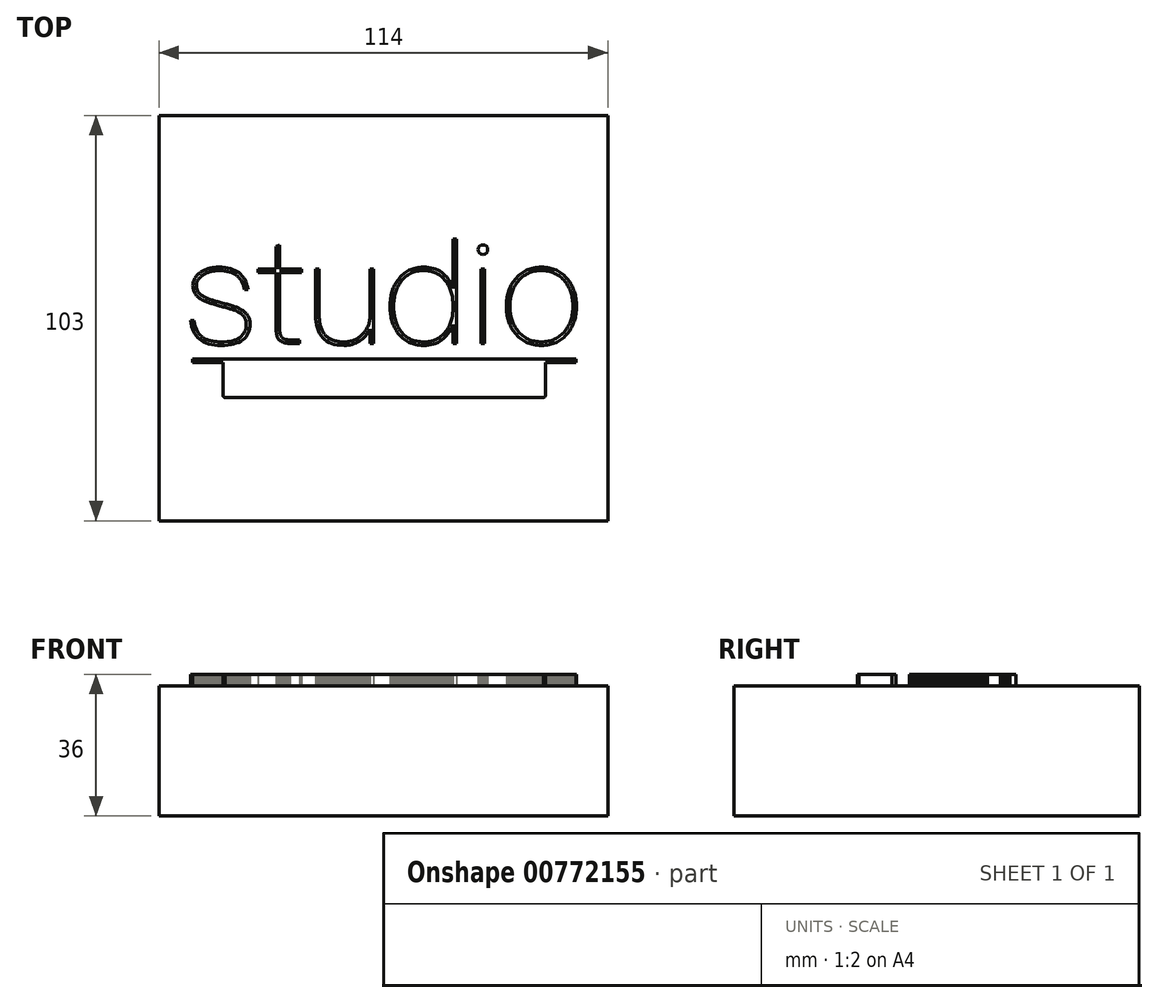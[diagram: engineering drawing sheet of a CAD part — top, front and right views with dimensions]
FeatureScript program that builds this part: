
annotation { "Feature Type Name" : "Feature", "Feature Type Description" : "" }
export const myFeature = defineFeature(function(context is Context, id is Id, definition is map)
    precondition{}
    {
        {
            var Q0;
            Q0=qCreatedBy(makeId("Top.planeOp"),FACE);
            var sketch = newSketch(context, id + "F0", { "sketchPlane" : qUnion([Q0])});
            skLineSegment(sketch, "E0", {"start": v(-48.1, -0.6) * mm, "end": v(-48.05, -0.96) * mm});
            skLineSegment(sketch, "E1", {"start": v(-48.05, -0.96) * mm, "end": v(-48, -1.3) * mm});
            skLineSegment(sketch, "E2", {"start": v(-48, -1.3) * mm, "end": v(-47.93, -1.64) * mm});
            skLineSegment(sketch, "E3", {"start": v(-47.93, -1.64) * mm, "end": v(-47.85, -1.96) * mm});
            skLineSegment(sketch, "E4", {"start": v(-47.85, -1.96) * mm, "end": v(-47.75, -2.27) * mm});
            skLineSegment(sketch, "E5", {"start": v(-47.75, -2.27) * mm, "end": v(-47.65, -2.56) * mm});
            skLineSegment(sketch, "E6", {"start": v(-47.65, -2.56) * mm, "end": v(-47.54, -2.85) * mm});
            skLineSegment(sketch, "E7", {"start": v(-47.54, -2.85) * mm, "end": v(-47.41, -3.12) * mm});
            skLineSegment(sketch, "E8", {"start": v(-47.41, -3.12) * mm, "end": v(-47.28, -3.38) * mm});
            skLineSegment(sketch, "E9", {"start": v(-47.28, -3.38) * mm, "end": v(-47.13, -3.62) * mm});
            skLineSegment(sketch, "E10", {"start": v(-47.13, -3.62) * mm, "end": v(-46.97, -3.86) * mm});
            skLineSegment(sketch, "E11", {"start": v(-46.97, -3.86) * mm, "end": v(-46.8, -4.08) * mm});
            skLineSegment(sketch, "E12", {"start": v(-46.8, -4.08) * mm, "end": v(-46.62, -4.29) * mm});
            skLineSegment(sketch, "E13", {"start": v(-46.62, -4.29) * mm, "end": v(-46.42, -4.48) * mm});
            skLineSegment(sketch, "E14", {"start": v(-46.42, -4.48) * mm, "end": v(-46.21, -4.67) * mm});
            skLineSegment(sketch, "E15", {"start": v(-46.21, -4.67) * mm, "end": v(-46, -4.84) * mm});
            skLineSegment(sketch, "E16", {"start": v(-46, -4.84) * mm, "end": v(-45.8, -4.98) * mm});
            skLineSegment(sketch, "E17", {"start": v(-45.8, -4.98) * mm, "end": v(-45.57, -5.12) * mm});
            skLineSegment(sketch, "E18", {"start": v(-45.57, -5.12) * mm, "end": v(-45.35, -5.25) * mm});
            skLineSegment(sketch, "E19", {"start": v(-45.35, -5.25) * mm, "end": v(-45.1, -5.36) * mm});
            skLineSegment(sketch, "E20", {"start": v(-45.1, -5.36) * mm, "end": v(-44.85, -5.47) * mm});
            skLineSegment(sketch, "E21", {"start": v(-44.85, -5.47) * mm, "end": v(-44.59, -5.57) * mm});
            skLineSegment(sketch, "E22", {"start": v(-44.59, -5.57) * mm, "end": v(-44.3, -5.66) * mm});
            skLineSegment(sketch, "E23", {"start": v(-44.3, -5.66) * mm, "end": v(-44.02, -5.74) * mm});
            skLineSegment(sketch, "E24", {"start": v(-44.02, -5.74) * mm, "end": v(-43.72, -5.81) * mm});
            skLineSegment(sketch, "E25", {"start": v(-43.72, -5.81) * mm, "end": v(-43.4, -5.87) * mm});
            skLineSegment(sketch, "E26", {"start": v(-43.4, -5.87) * mm, "end": v(-43.07, -5.92) * mm});
            skLineSegment(sketch, "E27", {"start": v(-43.07, -5.92) * mm, "end": v(-42.73, -5.97) * mm});
            skLineSegment(sketch, "E28", {"start": v(-42.73, -5.97) * mm, "end": v(-42.38, -6) * mm});
            skLineSegment(sketch, "E29", {"start": v(-42.38, -6) * mm, "end": v(-42.02, -6.02) * mm});
            skLineSegment(sketch, "E30", {"start": v(-42.02, -6.02) * mm, "end": v(-41.64, -6.04) * mm});
            skLineSegment(sketch, "E31", {"start": v(-41.64, -6.04) * mm, "end": v(-41.25, -6.04) * mm});
            skLineSegment(sketch, "E32", {"start": v(-41.25, -6.04) * mm, "end": v(-40.48, -6.02) * mm});
            skLineSegment(sketch, "E33", {"start": v(-40.48, -6.02) * mm, "end": v(-39.76, -5.97) * mm});
            skLineSegment(sketch, "E34", {"start": v(-39.76, -5.97) * mm, "end": v(-39.08, -5.88) * mm});
            skLineSegment(sketch, "E35", {"start": v(-39.08, -5.88) * mm, "end": v(-38.46, -5.75) * mm});
            skLineSegment(sketch, "E36", {"start": v(-38.46, -5.75) * mm, "end": v(-37.89, -5.58) * mm});
            skLineSegment(sketch, "E37", {"start": v(-37.89, -5.58) * mm, "end": v(-37.36, -5.38) * mm});
            skLineSegment(sketch, "E38", {"start": v(-37.36, -5.38) * mm, "end": v(-36.89, -5.14) * mm});
            skLineSegment(sketch, "E39", {"start": v(-36.89, -5.14) * mm, "end": v(-36.46, -4.87) * mm});
            skLineSegment(sketch, "E40", {"start": v(-36.46, -4.87) * mm, "end": v(-36.09, -4.56) * mm});
            skLineSegment(sketch, "E41", {"start": v(-36.09, -4.56) * mm, "end": v(-35.76, -4.21) * mm});
            skLineSegment(sketch, "E42", {"start": v(-35.76, -4.21) * mm, "end": v(-35.48, -3.83) * mm});
            skLineSegment(sketch, "E43", {"start": v(-35.48, -3.83) * mm, "end": v(-35.26, -3.41) * mm});
            skLineSegment(sketch, "E44", {"start": v(-35.26, -3.41) * mm, "end": v(-35.08, -2.95) * mm});
            skLineSegment(sketch, "E45", {"start": v(-35.08, -2.95) * mm, "end": v(-34.96, -2.46) * mm});
            skLineSegment(sketch, "E46", {"start": v(-34.96, -2.46) * mm, "end": v(-34.88, -1.94) * mm});
            skLineSegment(sketch, "E47", {"start": v(-34.88, -1.94) * mm, "end": v(-34.86, -1.37) * mm});
            skLineSegment(sketch, "E48", {"start": v(-34.86, -1.37) * mm, "end": v(-34.87, -1.13) * mm});
            skLineSegment(sketch, "E49", {"start": v(-34.87, -1.13) * mm, "end": v(-34.9, -0.9) * mm});
            skLineSegment(sketch, "E50", {"start": v(-34.9, -0.9) * mm, "end": v(-34.93, -0.67) * mm});
            skLineSegment(sketch, "E51", {"start": v(-34.93, -0.67) * mm, "end": v(-35, -0.45) * mm});
            skLineSegment(sketch, "E52", {"start": v(-35, -0.45) * mm, "end": v(-35.06, -0.24) * mm});
            skLineSegment(sketch, "E53", {"start": v(-35.06, -0.24) * mm, "end": v(-35.16, -0.03) * mm});
            skLineSegment(sketch, "E54", {"start": v(-35.16, -0.03) * mm, "end": v(-35.26, 0.17) * mm});
            skLineSegment(sketch, "E55", {"start": v(-35.26, 0.17) * mm, "end": v(-35.38, 0.36) * mm});
            skLineSegment(sketch, "E56", {"start": v(-35.38, 0.36) * mm, "end": v(-35.52, 0.54) * mm});
            skLineSegment(sketch, "E57", {"start": v(-35.52, 0.54) * mm, "end": v(-35.68, 0.71) * mm});
            skLineSegment(sketch, "E58", {"start": v(-35.68, 0.71) * mm, "end": v(-35.85, 0.88) * mm});
            skLineSegment(sketch, "E59", {"start": v(-35.85, 0.88) * mm, "end": v(-36.03, 1.04) * mm});
            skLineSegment(sketch, "E60", {"start": v(-36.03, 1.04) * mm, "end": v(-36.23, 1.2) * mm});
            skLineSegment(sketch, "E61", {"start": v(-36.23, 1.2) * mm, "end": v(-36.45, 1.34) * mm});
            skLineSegment(sketch, "E62", {"start": v(-36.45, 1.34) * mm, "end": v(-36.68, 1.48) * mm});
            skLineSegment(sketch, "E63", {"start": v(-36.68, 1.48) * mm, "end": v(-36.93, 1.62) * mm});
            skLineSegment(sketch, "E64", {"start": v(-36.93, 1.62) * mm, "end": v(-37.07, 1.69) * mm});
            skLineSegment(sketch, "E65", {"start": v(-37.07, 1.69) * mm, "end": v(-37.23, 1.76) * mm});
            skLineSegment(sketch, "E66", {"start": v(-37.23, 1.76) * mm, "end": v(-37.42, 1.84) * mm});
            skLineSegment(sketch, "E67", {"start": v(-37.42, 1.84) * mm, "end": v(-37.62, 1.92) * mm});
            skLineSegment(sketch, "E68", {"start": v(-37.62, 1.92) * mm, "end": v(-37.84, 2) * mm});
            skLineSegment(sketch, "E69", {"start": v(-37.84, 2) * mm, "end": v(-38.08, 2.09) * mm});
            skLineSegment(sketch, "E70", {"start": v(-38.08, 2.09) * mm, "end": v(-38.34, 2.18) * mm});
            skLineSegment(sketch, "E71", {"start": v(-38.34, 2.18) * mm, "end": v(-38.62, 2.27) * mm});
            skLineSegment(sketch, "E72", {"start": v(-38.62, 2.27) * mm, "end": v(-38.93, 2.37) * mm});
            skLineSegment(sketch, "E73", {"start": v(-38.93, 2.37) * mm, "end": v(-39.25, 2.46) * mm});
            skLineSegment(sketch, "E74", {"start": v(-39.25, 2.46) * mm, "end": v(-39.59, 2.57) * mm});
            skLineSegment(sketch, "E75", {"start": v(-39.59, 2.57) * mm, "end": v(-39.95, 2.67) * mm});
            skLineSegment(sketch, "E76", {"start": v(-39.95, 2.67) * mm, "end": v(-40.33, 2.78) * mm});
            skLineSegment(sketch, "E77", {"start": v(-40.33, 2.78) * mm, "end": v(-40.73, 2.89) * mm});
            skLineSegment(sketch, "E78", {"start": v(-40.73, 2.89) * mm, "end": v(-41.15, 3) * mm});
            skLineSegment(sketch, "E79", {"start": v(-41.15, 3) * mm, "end": v(-41.6, 3.11) * mm});
            skLineSegment(sketch, "E80", {"start": v(-41.6, 3.11) * mm, "end": v(-42, 3.22) * mm});
            skLineSegment(sketch, "E81", {"start": v(-42, 3.22) * mm, "end": v(-42.4, 3.33) * mm});
            skLineSegment(sketch, "E82", {"start": v(-42.4, 3.33) * mm, "end": v(-42.8, 3.44) * mm});
            skLineSegment(sketch, "E83", {"start": v(-42.8, 3.44) * mm, "end": v(-43.16, 3.55) * mm});
            skLineSegment(sketch, "E84", {"start": v(-43.16, 3.55) * mm, "end": v(-43.5, 3.66) * mm});
            skLineSegment(sketch, "E85", {"start": v(-43.5, 3.66) * mm, "end": v(-43.84, 3.77) * mm});
            skLineSegment(sketch, "E86", {"start": v(-43.84, 3.77) * mm, "end": v(-44.16, 3.87) * mm});
            skLineSegment(sketch, "E87", {"start": v(-44.16, 3.87) * mm, "end": v(-44.47, 3.98) * mm});
            skLineSegment(sketch, "E88", {"start": v(-44.47, 3.98) * mm, "end": v(-44.75, 4.09) * mm});
            skLineSegment(sketch, "E89", {"start": v(-44.75, 4.09) * mm, "end": v(-45.02, 4.2) * mm});
            skLineSegment(sketch, "E90", {"start": v(-45.02, 4.2) * mm, "end": v(-45.28, 4.3) * mm});
            skLineSegment(sketch, "E91", {"start": v(-45.28, 4.3) * mm, "end": v(-45.51, 4.4) * mm});
            skLineSegment(sketch, "E92", {"start": v(-45.51, 4.4) * mm, "end": v(-45.73, 4.5) * mm});
            skLineSegment(sketch, "E93", {"start": v(-45.73, 4.5) * mm, "end": v(-45.94, 4.6) * mm});
            skLineSegment(sketch, "E94", {"start": v(-45.94, 4.6) * mm, "end": v(-46.12, 4.7) * mm});
            skLineSegment(sketch, "E95", {"start": v(-46.12, 4.7) * mm, "end": v(-46.3, 4.8) * mm});
            skLineSegment(sketch, "E96", {"start": v(-46.3, 4.8) * mm, "end": v(-46.55, 4.95) * mm});
            skLineSegment(sketch, "E97", {"start": v(-46.55, 4.95) * mm, "end": v(-46.8, 5.12) * mm});
            skLineSegment(sketch, "E98", {"start": v(-46.8, 5.12) * mm, "end": v(-47.02, 5.3) * mm});
            skLineSegment(sketch, "E99", {"start": v(-47.02, 5.3) * mm, "end": v(-47.23, 5.48) * mm});
            skLineSegment(sketch, "E100", {"start": v(-47.23, 5.48) * mm, "end": v(-47.43, 5.67) * mm});
            skLineSegment(sketch, "E101", {"start": v(-47.43, 5.67) * mm, "end": v(-47.6, 5.87) * mm});
            skLineSegment(sketch, "E102", {"start": v(-47.6, 5.87) * mm, "end": v(-47.76, 6.08) * mm});
            skLineSegment(sketch, "E103", {"start": v(-47.76, 6.08) * mm, "end": v(-47.9, 6.3) * mm});
            skLineSegment(sketch, "E104", {"start": v(-47.9, 6.3) * mm, "end": v(-48.03, 6.51) * mm});
            skLineSegment(sketch, "E105", {"start": v(-48.03, 6.51) * mm, "end": v(-48.14, 6.74) * mm});
            skLineSegment(sketch, "E106", {"start": v(-48.14, 6.74) * mm, "end": v(-48.23, 6.98) * mm});
            skLineSegment(sketch, "E107", {"start": v(-48.23, 6.98) * mm, "end": v(-48.3, 7.22) * mm});
            skLineSegment(sketch, "E108", {"start": v(-48.3, 7.22) * mm, "end": v(-48.36, 7.47) * mm});
            skLineSegment(sketch, "E109", {"start": v(-48.36, 7.47) * mm, "end": v(-48.4, 7.72) * mm});
            skLineSegment(sketch, "E110", {"start": v(-48.4, 7.72) * mm, "end": v(-48.43, 7.99) * mm});
            skLineSegment(sketch, "E111", {"start": v(-48.43, 7.99) * mm, "end": v(-48.44, 8.26) * mm});
            skLineSegment(sketch, "E112", {"start": v(-48.44, 8.26) * mm, "end": v(-48.43, 8.51) * mm});
            skLineSegment(sketch, "E113", {"start": v(-48.43, 8.51) * mm, "end": v(-48.4, 8.77) * mm});
            skLineSegment(sketch, "E114", {"start": v(-48.4, 8.77) * mm, "end": v(-48.37, 9.01) * mm});
            skLineSegment(sketch, "E115", {"start": v(-48.37, 9.01) * mm, "end": v(-48.31, 9.25) * mm});
            skLineSegment(sketch, "E116", {"start": v(-48.31, 9.25) * mm, "end": v(-48.24, 9.49) * mm});
            skLineSegment(sketch, "E117", {"start": v(-48.24, 9.49) * mm, "end": v(-48.15, 9.72) * mm});
            skLineSegment(sketch, "E118", {"start": v(-48.15, 9.72) * mm, "end": v(-48.05, 9.94) * mm});
            skLineSegment(sketch, "E119", {"start": v(-48.05, 9.94) * mm, "end": v(-47.93, 10.16) * mm});
            skLineSegment(sketch, "E120", {"start": v(-47.93, 10.16) * mm, "end": v(-47.8, 10.37) * mm});
            skLineSegment(sketch, "E121", {"start": v(-47.8, 10.37) * mm, "end": v(-47.65, 10.58) * mm});
            skLineSegment(sketch, "E122", {"start": v(-47.65, 10.58) * mm, "end": v(-47.48, 10.78) * mm});
            skLineSegment(sketch, "E123", {"start": v(-47.48, 10.78) * mm, "end": v(-47.3, 10.97) * mm});
            skLineSegment(sketch, "E124", {"start": v(-47.3, 10.97) * mm, "end": v(-47.1, 11.16) * mm});
            skLineSegment(sketch, "E125", {"start": v(-47.1, 11.16) * mm, "end": v(-46.88, 11.34) * mm});
            skLineSegment(sketch, "E126", {"start": v(-46.88, 11.34) * mm, "end": v(-46.65, 11.52) * mm});
            skLineSegment(sketch, "E127", {"start": v(-46.65, 11.52) * mm, "end": v(-46.4, 11.68) * mm});
            skLineSegment(sketch, "E128", {"start": v(-46.4, 11.68) * mm, "end": v(-46.16, 11.84) * mm});
            skLineSegment(sketch, "E129", {"start": v(-46.16, 11.84) * mm, "end": v(-45.92, 12) * mm});
            skLineSegment(sketch, "E130", {"start": v(-45.92, 12) * mm, "end": v(-45.66, 12.13) * mm});
            skLineSegment(sketch, "E131", {"start": v(-45.66, 12.13) * mm, "end": v(-45.4, 12.25) * mm});
            skLineSegment(sketch, "E132", {"start": v(-45.4, 12.25) * mm, "end": v(-45.13, 12.37) * mm});
            skLineSegment(sketch, "E133", {"start": v(-45.13, 12.37) * mm, "end": v(-44.86, 12.47) * mm});
            skLineSegment(sketch, "E134", {"start": v(-44.86, 12.47) * mm, "end": v(-44.58, 12.57) * mm});
            skLineSegment(sketch, "E135", {"start": v(-44.58, 12.57) * mm, "end": v(-44.3, 12.65) * mm});
            skLineSegment(sketch, "E136", {"start": v(-44.3, 12.65) * mm, "end": v(-44, 12.72) * mm});
            skLineSegment(sketch, "E137", {"start": v(-44, 12.72) * mm, "end": v(-43.7, 12.79) * mm});
            skLineSegment(sketch, "E138", {"start": v(-43.7, 12.79) * mm, "end": v(-43.4, 12.84) * mm});
            skLineSegment(sketch, "E139", {"start": v(-43.4, 12.84) * mm, "end": v(-43.09, 12.89) * mm});
            skLineSegment(sketch, "E140", {"start": v(-43.09, 12.89) * mm, "end": v(-42.77, 12.92) * mm});
            skLineSegment(sketch, "E141", {"start": v(-42.77, 12.92) * mm, "end": v(-42.45, 12.94) * mm});
            skLineSegment(sketch, "E142", {"start": v(-42.45, 12.94) * mm, "end": v(-42.12, 12.96) * mm});
            skLineSegment(sketch, "E143", {"start": v(-42.12, 12.96) * mm, "end": v(-41.78, 12.96) * mm});
            skLineSegment(sketch, "E144", {"start": v(-41.78, 12.96) * mm, "end": v(-41, 12.94) * mm});
            skLineSegment(sketch, "E145", {"start": v(-41, 12.94) * mm, "end": v(-40.26, 12.87) * mm});
            skLineSegment(sketch, "E146", {"start": v(-40.26, 12.87) * mm, "end": v(-39.56, 12.76) * mm});
            skLineSegment(sketch, "E147", {"start": v(-39.56, 12.76) * mm, "end": v(-38.9, 12.6) * mm});
            skLineSegment(sketch, "E148", {"start": v(-38.9, 12.6) * mm, "end": v(-38.3, 12.4) * mm});
            skLineSegment(sketch, "E149", {"start": v(-38.3, 12.4) * mm, "end": v(-37.73, 12.16) * mm});
            skLineSegment(sketch, "E150", {"start": v(-37.73, 12.16) * mm, "end": v(-37.2, 11.87) * mm});
            skLineSegment(sketch, "E151", {"start": v(-37.2, 11.87) * mm, "end": v(-36.73, 11.54) * mm});
            skLineSegment(sketch, "E152", {"start": v(-36.73, 11.54) * mm, "end": v(-36.3, 11.16) * mm});
            skLineSegment(sketch, "E153", {"start": v(-36.3, 11.16) * mm, "end": v(-35.9, 10.74) * mm});
            skLineSegment(sketch, "E154", {"start": v(-35.9, 10.74) * mm, "end": v(-35.55, 10.27) * mm});
            skLineSegment(sketch, "E155", {"start": v(-35.55, 10.27) * mm, "end": v(-35.24, 9.76) * mm});
            skLineSegment(sketch, "E156", {"start": v(-35.24, 9.76) * mm, "end": v(-34.98, 9.2) * mm});
            skLineSegment(sketch, "E157", {"start": v(-34.98, 9.2) * mm, "end": v(-34.76, 8.6) * mm});
            skLineSegment(sketch, "E158", {"start": v(-34.76, 8.6) * mm, "end": v(-34.58, 7.96) * mm});
            skLineSegment(sketch, "E159", {"start": v(-34.58, 7.96) * mm, "end": v(-34.44, 7.27) * mm});
            skLineSegment(sketch, "E160", {"start": v(-34.44, 7.27) * mm, "end": v(-35.35, 7.27) * mm});
            skLineSegment(sketch, "E161", {"start": v(-35.35, 7.27) * mm, "end": v(-35.4, 7.55) * mm});
            skLineSegment(sketch, "E162", {"start": v(-35.4, 7.55) * mm, "end": v(-35.46, 7.83) * mm});
            skLineSegment(sketch, "E163", {"start": v(-35.46, 7.83) * mm, "end": v(-35.53, 8.1) * mm});
            skLineSegment(sketch, "E164", {"start": v(-35.53, 8.1) * mm, "end": v(-35.6, 8.35) * mm});
            skLineSegment(sketch, "E165", {"start": v(-35.6, 8.35) * mm, "end": v(-35.7, 8.6) * mm});
            skLineSegment(sketch, "E166", {"start": v(-35.7, 8.6) * mm, "end": v(-35.79, 8.83) * mm});
            skLineSegment(sketch, "E167", {"start": v(-35.79, 8.83) * mm, "end": v(-35.89, 9.06) * mm});
            skLineSegment(sketch, "E168", {"start": v(-35.89, 9.06) * mm, "end": v(-36, 9.28) * mm});
            skLineSegment(sketch, "E169", {"start": v(-36, 9.28) * mm, "end": v(-36.11, 9.49) * mm});
            skLineSegment(sketch, "E170", {"start": v(-36.11, 9.49) * mm, "end": v(-36.24, 9.7) * mm});
            skLineSegment(sketch, "E171", {"start": v(-36.24, 9.7) * mm, "end": v(-36.37, 9.89) * mm});
            skLineSegment(sketch, "E172", {"start": v(-36.37, 9.89) * mm, "end": v(-36.51, 10.07) * mm});
            skLineSegment(sketch, "E173", {"start": v(-36.51, 10.07) * mm, "end": v(-36.66, 10.25) * mm});
            skLineSegment(sketch, "E174", {"start": v(-36.66, 10.25) * mm, "end": v(-36.82, 10.42) * mm});
            skLineSegment(sketch, "E175", {"start": v(-36.82, 10.42) * mm, "end": v(-36.98, 10.58) * mm});
            skLineSegment(sketch, "E176", {"start": v(-36.98, 10.58) * mm, "end": v(-37.15, 10.74) * mm});
            skLineSegment(sketch, "E177", {"start": v(-37.15, 10.74) * mm, "end": v(-37.37, 10.9) * mm});
            skLineSegment(sketch, "E178", {"start": v(-37.37, 10.9) * mm, "end": v(-37.6, 11.06) * mm});
            skLineSegment(sketch, "E179", {"start": v(-37.6, 11.06) * mm, "end": v(-37.83, 11.2) * mm});
            skLineSegment(sketch, "E180", {"start": v(-37.83, 11.2) * mm, "end": v(-38.08, 11.33) * mm});
            skLineSegment(sketch, "E181", {"start": v(-38.08, 11.33) * mm, "end": v(-38.33, 11.45) * mm});
            skLineSegment(sketch, "E182", {"start": v(-38.33, 11.45) * mm, "end": v(-38.6, 11.56) * mm});
            skLineSegment(sketch, "E183", {"start": v(-38.6, 11.56) * mm, "end": v(-38.87, 11.66) * mm});
            skLineSegment(sketch, "E184", {"start": v(-38.87, 11.66) * mm, "end": v(-39.16, 11.75) * mm});
            skLineSegment(sketch, "E185", {"start": v(-39.16, 11.75) * mm, "end": v(-39.45, 11.83) * mm});
            skLineSegment(sketch, "E186", {"start": v(-39.45, 11.83) * mm, "end": v(-39.75, 11.9) * mm});
            skLineSegment(sketch, "E187", {"start": v(-39.75, 11.9) * mm, "end": v(-40.07, 11.96) * mm});
            skLineSegment(sketch, "E188", {"start": v(-40.07, 11.96) * mm, "end": v(-40.4, 12) * mm});
            skLineSegment(sketch, "E189", {"start": v(-40.4, 12) * mm, "end": v(-40.72, 12.04) * mm});
            skLineSegment(sketch, "E190", {"start": v(-40.72, 12.04) * mm, "end": v(-41.07, 12.07) * mm});
            skLineSegment(sketch, "E191", {"start": v(-41.07, 12.07) * mm, "end": v(-41.42, 12.08) * mm});
            skLineSegment(sketch, "E192", {"start": v(-41.42, 12.08) * mm, "end": v(-41.78, 12.09) * mm});
            skLineSegment(sketch, "E193", {"start": v(-41.78, 12.09) * mm, "end": v(-42.09, 12.08) * mm});
            skLineSegment(sketch, "E194", {"start": v(-42.09, 12.08) * mm, "end": v(-42.39, 12.07) * mm});
            skLineSegment(sketch, "E195", {"start": v(-42.39, 12.07) * mm, "end": v(-42.68, 12.05) * mm});
            skLineSegment(sketch, "E196", {"start": v(-42.68, 12.05) * mm, "end": v(-42.97, 12.02) * mm});
            skLineSegment(sketch, "E197", {"start": v(-42.97, 12.02) * mm, "end": v(-43.25, 11.98) * mm});
            skLineSegment(sketch, "E198", {"start": v(-43.25, 11.98) * mm, "end": v(-43.52, 11.93) * mm});
            skLineSegment(sketch, "E199", {"start": v(-43.52, 11.93) * mm, "end": v(-43.78, 11.87) * mm});
            skLineSegment(sketch, "E200", {"start": v(-43.78, 11.87) * mm, "end": v(-44.04, 11.8) * mm});
            skLineSegment(sketch, "E201", {"start": v(-44.04, 11.8) * mm, "end": v(-44.3, 11.73) * mm});
            skLineSegment(sketch, "E202", {"start": v(-44.3, 11.73) * mm, "end": v(-44.54, 11.65) * mm});
            skLineSegment(sketch, "E203", {"start": v(-44.54, 11.65) * mm, "end": v(-44.78, 11.56) * mm});
            skLineSegment(sketch, "E204", {"start": v(-44.78, 11.56) * mm, "end": v(-45.01, 11.46) * mm});
            skLineSegment(sketch, "E205", {"start": v(-45.01, 11.46) * mm, "end": v(-45.24, 11.34) * mm});
            skLineSegment(sketch, "E206", {"start": v(-45.24, 11.34) * mm, "end": v(-45.46, 11.22) * mm});
            skLineSegment(sketch, "E207", {"start": v(-45.46, 11.22) * mm, "end": v(-45.67, 11.1) * mm});
            skLineSegment(sketch, "E208", {"start": v(-45.67, 11.1) * mm, "end": v(-45.88, 10.96) * mm});
            skLineSegment(sketch, "E209", {"start": v(-45.88, 10.96) * mm, "end": v(-46.09, 10.82) * mm});
            skLineSegment(sketch, "E210", {"start": v(-46.09, 10.82) * mm, "end": v(-46.28, 10.67) * mm});
            skLineSegment(sketch, "E211", {"start": v(-46.28, 10.67) * mm, "end": v(-46.45, 10.53) * mm});
            skLineSegment(sketch, "E212", {"start": v(-46.45, 10.53) * mm, "end": v(-46.62, 10.38) * mm});
            skLineSegment(sketch, "E213", {"start": v(-46.62, 10.38) * mm, "end": v(-46.77, 10.23) * mm});
            skLineSegment(sketch, "E214", {"start": v(-46.77, 10.23) * mm, "end": v(-46.9, 10.07) * mm});
            skLineSegment(sketch, "E215", {"start": v(-46.9, 10.07) * mm, "end": v(-47.02, 9.9) * mm});
            skLineSegment(sketch, "E216", {"start": v(-47.02, 9.9) * mm, "end": v(-47.13, 9.74) * mm});
            skLineSegment(sketch, "E217", {"start": v(-47.13, 9.74) * mm, "end": v(-47.23, 9.57) * mm});
            skLineSegment(sketch, "E218", {"start": v(-47.23, 9.57) * mm, "end": v(-47.31, 9.4) * mm});
            skLineSegment(sketch, "E219", {"start": v(-47.31, 9.4) * mm, "end": v(-47.38, 9.22) * mm});
            skLineSegment(sketch, "E220", {"start": v(-47.38, 9.22) * mm, "end": v(-47.44, 9.04) * mm});
            skLineSegment(sketch, "E221", {"start": v(-47.44, 9.04) * mm, "end": v(-47.48, 8.85) * mm});
            skLineSegment(sketch, "E222", {"start": v(-47.48, 8.85) * mm, "end": v(-47.51, 8.66) * mm});
            skLineSegment(sketch, "E223", {"start": v(-47.51, 8.66) * mm, "end": v(-47.53, 8.46) * mm});
            skLineSegment(sketch, "E224", {"start": v(-47.53, 8.46) * mm, "end": v(-47.54, 8.26) * mm});
            skLineSegment(sketch, "E225", {"start": v(-47.54, 8.26) * mm, "end": v(-47.53, 8.04) * mm});
            skLineSegment(sketch, "E226", {"start": v(-47.53, 8.04) * mm, "end": v(-47.5, 7.83) * mm});
            skLineSegment(sketch, "E227", {"start": v(-47.5, 7.83) * mm, "end": v(-47.47, 7.63) * mm});
            skLineSegment(sketch, "E228", {"start": v(-47.47, 7.63) * mm, "end": v(-47.42, 7.43) * mm});
            skLineSegment(sketch, "E229", {"start": v(-47.42, 7.43) * mm, "end": v(-47.36, 7.23) * mm});
            skLineSegment(sketch, "E230", {"start": v(-47.36, 7.23) * mm, "end": v(-47.28, 7.05) * mm});
            skLineSegment(sketch, "E231", {"start": v(-47.28, 7.05) * mm, "end": v(-47.18, 6.87) * mm});
            skLineSegment(sketch, "E232", {"start": v(-47.18, 6.87) * mm, "end": v(-47.08, 6.69) * mm});
            skLineSegment(sketch, "E233", {"start": v(-47.08, 6.69) * mm, "end": v(-46.95, 6.52) * mm});
            skLineSegment(sketch, "E234", {"start": v(-46.95, 6.52) * mm, "end": v(-46.81, 6.35) * mm});
            skLineSegment(sketch, "E235", {"start": v(-46.81, 6.35) * mm, "end": v(-46.66, 6.19) * mm});
            skLineSegment(sketch, "E236", {"start": v(-46.66, 6.19) * mm, "end": v(-46.49, 6.03) * mm});
            skLineSegment(sketch, "E237", {"start": v(-46.49, 6.03) * mm, "end": v(-46.3, 5.88) * mm});
            skLineSegment(sketch, "E238", {"start": v(-46.3, 5.88) * mm, "end": v(-46.1, 5.73) * mm});
            skLineSegment(sketch, "E239", {"start": v(-46.1, 5.73) * mm, "end": v(-45.89, 5.59) * mm});
            skLineSegment(sketch, "E240", {"start": v(-45.89, 5.59) * mm, "end": v(-45.66, 5.45) * mm});
            skLineSegment(sketch, "E241", {"start": v(-45.66, 5.45) * mm, "end": v(-45.5, 5.37) * mm});
            skLineSegment(sketch, "E242", {"start": v(-45.5, 5.37) * mm, "end": v(-45.33, 5.28) * mm});
            skLineSegment(sketch, "E243", {"start": v(-45.33, 5.28) * mm, "end": v(-45.14, 5.2) * mm});
            skLineSegment(sketch, "E244", {"start": v(-45.14, 5.2) * mm, "end": v(-44.94, 5.1) * mm});
            skLineSegment(sketch, "E245", {"start": v(-44.94, 5.1) * mm, "end": v(-44.73, 5.02) * mm});
            skLineSegment(sketch, "E246", {"start": v(-44.73, 5.02) * mm, "end": v(-44.5, 4.93) * mm});
            skLineSegment(sketch, "E247", {"start": v(-44.5, 4.93) * mm, "end": v(-44.25, 4.84) * mm});
            skLineSegment(sketch, "E248", {"start": v(-44.25, 4.84) * mm, "end": v(-44, 4.75) * mm});
            skLineSegment(sketch, "E249", {"start": v(-44, 4.75) * mm, "end": v(-43.72, 4.65) * mm});
            skLineSegment(sketch, "E250", {"start": v(-43.72, 4.65) * mm, "end": v(-43.43, 4.56) * mm});
            skLineSegment(sketch, "E251", {"start": v(-43.43, 4.56) * mm, "end": v(-43.13, 4.47) * mm});
            skLineSegment(sketch, "E252", {"start": v(-43.13, 4.47) * mm, "end": v(-42.81, 4.37) * mm});
            skLineSegment(sketch, "E253", {"start": v(-42.81, 4.37) * mm, "end": v(-42.48, 4.28) * mm});
            skLineSegment(sketch, "E254", {"start": v(-42.48, 4.28) * mm, "end": v(-42.14, 4.18) * mm});
            skLineSegment(sketch, "E255", {"start": v(-42.14, 4.18) * mm, "end": v(-41.78, 4.08) * mm});
            skLineSegment(sketch, "E256", {"start": v(-41.78, 4.08) * mm, "end": v(-41.4, 3.99) * mm});
            skLineSegment(sketch, "E257", {"start": v(-41.4, 3.99) * mm, "end": v(-40.95, 3.87) * mm});
            skLineSegment(sketch, "E258", {"start": v(-40.95, 3.87) * mm, "end": v(-40.5, 3.76) * mm});
            skLineSegment(sketch, "E259", {"start": v(-40.5, 3.76) * mm, "end": v(-40.09, 3.64) * mm});
            skLineSegment(sketch, "E260", {"start": v(-40.09, 3.64) * mm, "end": v(-39.68, 3.53) * mm});
            skLineSegment(sketch, "E261", {"start": v(-39.68, 3.53) * mm, "end": v(-39.3, 3.42) * mm});
            skLineSegment(sketch, "E262", {"start": v(-39.3, 3.42) * mm, "end": v(-38.93, 3.3) * mm});
            skLineSegment(sketch, "E263", {"start": v(-38.93, 3.3) * mm, "end": v(-38.58, 3.2) * mm});
            skLineSegment(sketch, "E264", {"start": v(-38.58, 3.2) * mm, "end": v(-38.25, 3.1) * mm});
            skLineSegment(sketch, "E265", {"start": v(-38.25, 3.1) * mm, "end": v(-37.94, 2.98) * mm});
            skLineSegment(sketch, "E266", {"start": v(-37.94, 2.98) * mm, "end": v(-37.65, 2.88) * mm});
            skLineSegment(sketch, "E267", {"start": v(-37.65, 2.88) * mm, "end": v(-37.37, 2.77) * mm});
            skLineSegment(sketch, "E268", {"start": v(-37.37, 2.77) * mm, "end": v(-37.12, 2.67) * mm});
            skLineSegment(sketch, "E269", {"start": v(-37.12, 2.67) * mm, "end": v(-36.88, 2.57) * mm});
            skLineSegment(sketch, "E270", {"start": v(-36.88, 2.57) * mm, "end": v(-36.66, 2.47) * mm});
            skLineSegment(sketch, "E271", {"start": v(-36.66, 2.47) * mm, "end": v(-36.47, 2.37) * mm});
            skLineSegment(sketch, "E272", {"start": v(-36.47, 2.37) * mm, "end": v(-36.29, 2.27) * mm});
            skLineSegment(sketch, "E273", {"start": v(-36.29, 2.27) * mm, "end": v(-36, 2.1) * mm});
            skLineSegment(sketch, "E274", {"start": v(-36, 2.1) * mm, "end": v(-35.73, 1.93) * mm});
            skLineSegment(sketch, "E275", {"start": v(-35.73, 1.93) * mm, "end": v(-35.48, 1.75) * mm});
            skLineSegment(sketch, "E276", {"start": v(-35.48, 1.75) * mm, "end": v(-35.25, 1.56) * mm});
            skLineSegment(sketch, "E277", {"start": v(-35.25, 1.56) * mm, "end": v(-35.04, 1.36) * mm});
            skLineSegment(sketch, "E278", {"start": v(-35.04, 1.36) * mm, "end": v(-34.84, 1.15) * mm});
            skLineSegment(sketch, "E279", {"start": v(-34.84, 1.15) * mm, "end": v(-34.67, 0.93) * mm});
            skLineSegment(sketch, "E280", {"start": v(-34.67, 0.93) * mm, "end": v(-34.5, 0.71) * mm});
            skLineSegment(sketch, "E281", {"start": v(-34.5, 0.71) * mm, "end": v(-34.37, 0.48) * mm});
            skLineSegment(sketch, "E282", {"start": v(-34.37, 0.48) * mm, "end": v(-34.25, 0.24) * mm});
            skLineSegment(sketch, "E283", {"start": v(-34.25, 0.24) * mm, "end": v(-34.15, 0) * mm});
            skLineSegment(sketch, "E284", {"start": v(-34.15, 0) * mm, "end": v(-34.07, -0.26) * mm});
            skLineSegment(sketch, "E285", {"start": v(-34.07, -0.26) * mm, "end": v(-34, -0.53) * mm});
            skLineSegment(sketch, "E286", {"start": v(-34, -0.53) * mm, "end": v(-33.95, -0.8) * mm});
            skLineSegment(sketch, "E287", {"start": v(-33.95, -0.8) * mm, "end": v(-33.93, -1.08) * mm});
            skLineSegment(sketch, "E288", {"start": v(-33.93, -1.08) * mm, "end": v(-33.92, -1.37) * mm});
            skLineSegment(sketch, "E289", {"start": v(-33.92, -1.37) * mm, "end": v(-33.95, -2.04) * mm});
            skLineSegment(sketch, "E290", {"start": v(-33.95, -2.04) * mm, "end": v(-34.03, -2.67) * mm});
            skLineSegment(sketch, "E291", {"start": v(-34.03, -2.67) * mm, "end": v(-34.17, -3.25) * mm});
            skLineSegment(sketch, "E292", {"start": v(-34.17, -3.25) * mm, "end": v(-34.38, -3.8) * mm});
            skLineSegment(sketch, "E293", {"start": v(-34.38, -3.8) * mm, "end": v(-34.63, -4.3) * mm});
            skLineSegment(sketch, "E294", {"start": v(-34.63, -4.3) * mm, "end": v(-34.95, -4.75) * mm});
            skLineSegment(sketch, "E295", {"start": v(-34.95, -4.75) * mm, "end": v(-35.32, -5.16) * mm});
            skLineSegment(sketch, "E296", {"start": v(-35.32, -5.16) * mm, "end": v(-35.75, -5.53) * mm});
            skLineSegment(sketch, "E297", {"start": v(-35.75, -5.53) * mm, "end": v(-36.24, -5.85) * mm});
            skLineSegment(sketch, "E298", {"start": v(-36.24, -5.85) * mm, "end": v(-36.78, -6.13) * mm});
            skLineSegment(sketch, "E299", {"start": v(-36.78, -6.13) * mm, "end": v(-37.38, -6.37) * mm});
            skLineSegment(sketch, "E300", {"start": v(-37.38, -6.37) * mm, "end": v(-38.04, -6.57) * mm});
            skLineSegment(sketch, "E301", {"start": v(-38.04, -6.57) * mm, "end": v(-38.76, -6.72) * mm});
            skLineSegment(sketch, "E302", {"start": v(-38.76, -6.72) * mm, "end": v(-39.53, -6.83) * mm});
            skLineSegment(sketch, "E303", {"start": v(-39.53, -6.83) * mm, "end": v(-40.37, -6.9) * mm});
            skLineSegment(sketch, "E304", {"start": v(-40.37, -6.9) * mm, "end": v(-41.25, -6.92) * mm});
            skLineSegment(sketch, "E305", {"start": v(-41.25, -6.92) * mm, "end": v(-42.12, -6.9) * mm});
            skLineSegment(sketch, "E306", {"start": v(-42.12, -6.9) * mm, "end": v(-42.93, -6.82) * mm});
            skLineSegment(sketch, "E307", {"start": v(-42.93, -6.82) * mm, "end": v(-43.7, -6.7) * mm});
            skLineSegment(sketch, "E308", {"start": v(-43.7, -6.7) * mm, "end": v(-44.4, -6.52) * mm});
            skLineSegment(sketch, "E309", {"start": v(-44.4, -6.52) * mm, "end": v(-45.07, -6.3) * mm});
            skLineSegment(sketch, "E310", {"start": v(-45.07, -6.3) * mm, "end": v(-45.68, -6.03) * mm});
            skLineSegment(sketch, "E311", {"start": v(-45.68, -6.03) * mm, "end": v(-46.24, -5.7) * mm});
            skLineSegment(sketch, "E312", {"start": v(-46.24, -5.7) * mm, "end": v(-46.76, -5.33) * mm});
            skLineSegment(sketch, "E313", {"start": v(-46.76, -5.33) * mm, "end": v(-47.22, -4.92) * mm});
            skLineSegment(sketch, "E314", {"start": v(-47.22, -4.92) * mm, "end": v(-47.63, -4.45) * mm});
            skLineSegment(sketch, "E315", {"start": v(-47.63, -4.45) * mm, "end": v(-47.99, -3.93) * mm});
            skLineSegment(sketch, "E316", {"start": v(-47.99, -3.93) * mm, "end": v(-48.3, -3.36) * mm});
            skLineSegment(sketch, "E317", {"start": v(-48.3, -3.36) * mm, "end": v(-48.56, -2.75) * mm});
            skLineSegment(sketch, "E318", {"start": v(-48.56, -2.75) * mm, "end": v(-48.77, -2.08) * mm});
            skLineSegment(sketch, "E319", {"start": v(-48.77, -2.08) * mm, "end": v(-48.93, -1.37) * mm});
            skLineSegment(sketch, "E320", {"start": v(-48.93, -1.37) * mm, "end": v(-49.04, -0.6) * mm});
            skLineSegment(sketch, "E321", {"start": v(-49.04, -0.6) * mm, "end": v(-48.1, -0.6) * mm});
            skLineSegment(sketch, "E322", {"start": v(-23.53, -6.4) * mm, "end": v(-23.68, -6.4) * mm});
            skLineSegment(sketch, "E323", {"start": v(-23.68, -6.4) * mm, "end": v(-23.95, -6.4) * mm});
            skLineSegment(sketch, "E324", {"start": v(-23.95, -6.4) * mm, "end": v(-24.2, -6.39) * mm});
            skLineSegment(sketch, "E325", {"start": v(-24.2, -6.39) * mm, "end": v(-24.44, -6.37) * mm});
            skLineSegment(sketch, "E326", {"start": v(-24.44, -6.37) * mm, "end": v(-24.67, -6.34) * mm});
            skLineSegment(sketch, "E327", {"start": v(-24.67, -6.34) * mm, "end": v(-24.9, -6.3) * mm});
            skLineSegment(sketch, "E328", {"start": v(-24.9, -6.3) * mm, "end": v(-25.1, -6.26) * mm});
            skLineSegment(sketch, "E329", {"start": v(-25.1, -6.26) * mm, "end": v(-25.3, -6.2) * mm});
            skLineSegment(sketch, "E330", {"start": v(-25.3, -6.2) * mm, "end": v(-25.49, -6.14) * mm});
            skLineSegment(sketch, "E331", {"start": v(-25.49, -6.14) * mm, "end": v(-25.67, -6.07) * mm});
            skLineSegment(sketch, "E332", {"start": v(-25.67, -6.07) * mm, "end": v(-25.84, -6) * mm});
            skLineSegment(sketch, "E333", {"start": v(-25.84, -6) * mm, "end": v(-26, -5.91) * mm});
            skLineSegment(sketch, "E334", {"start": v(-26, -5.91) * mm, "end": v(-26.14, -5.82) * mm});
            skLineSegment(sketch, "E335", {"start": v(-26.14, -5.82) * mm, "end": v(-26.27, -5.72) * mm});
            skLineSegment(sketch, "E336", {"start": v(-26.27, -5.72) * mm, "end": v(-26.4, -5.62) * mm});
            skLineSegment(sketch, "E337", {"start": v(-26.4, -5.62) * mm, "end": v(-26.51, -5.5) * mm});
            skLineSegment(sketch, "E338", {"start": v(-26.51, -5.5) * mm, "end": v(-26.62, -5.39) * mm});
            skLineSegment(sketch, "E339", {"start": v(-26.62, -5.39) * mm, "end": v(-26.7, -5.27) * mm});
            skLineSegment(sketch, "E340", {"start": v(-26.7, -5.27) * mm, "end": v(-26.78, -5.15) * mm});
            skLineSegment(sketch, "E341", {"start": v(-26.78, -5.15) * mm, "end": v(-26.85, -5.02) * mm});
            skLineSegment(sketch, "E342", {"start": v(-26.85, -5.02) * mm, "end": v(-26.91, -4.88) * mm});
            skLineSegment(sketch, "E343", {"start": v(-26.91, -4.88) * mm, "end": v(-26.98, -4.73) * mm});
            skLineSegment(sketch, "E344", {"start": v(-26.98, -4.73) * mm, "end": v(-27.03, -4.58) * mm});
            skLineSegment(sketch, "E345", {"start": v(-27.03, -4.58) * mm, "end": v(-27.08, -4.41) * mm});
            skLineSegment(sketch, "E346", {"start": v(-27.08, -4.41) * mm, "end": v(-27.13, -4.24) * mm});
            skLineSegment(sketch, "E347", {"start": v(-27.13, -4.24) * mm, "end": v(-27.17, -4.06) * mm});
            skLineSegment(sketch, "E348", {"start": v(-27.17, -4.06) * mm, "end": v(-27.2, -3.87) * mm});
            skLineSegment(sketch, "E349", {"start": v(-27.2, -3.87) * mm, "end": v(-27.23, -3.68) * mm});
            skLineSegment(sketch, "E350", {"start": v(-27.23, -3.68) * mm, "end": v(-27.25, -3.47) * mm});
            skLineSegment(sketch, "E351", {"start": v(-27.25, -3.47) * mm, "end": v(-27.27, -3.26) * mm});
            skLineSegment(sketch, "E352", {"start": v(-27.27, -3.26) * mm, "end": v(-27.28, -3.04) * mm});
            skLineSegment(sketch, "E353", {"start": v(-27.28, -3.04) * mm, "end": v(-27.3, -2.81) * mm});
            skLineSegment(sketch, "E354", {"start": v(-27.3, -2.81) * mm, "end": v(-27.3, -2.58) * mm});
            skLineSegment(sketch, "E355", {"start": v(-27.3, -2.58) * mm, "end": v(-27.3, -1.7) * mm});
            skLineSegment(sketch, "E356", {"start": v(-27.3, -1.7) * mm, "end": v(-27.3, 11.58) * mm});
            skLineSegment(sketch, "E357", {"start": v(-27.3, 11.58) * mm, "end": v(-31.85, 11.58) * mm});
            skLineSegment(sketch, "E358", {"start": v(-31.85, 11.58) * mm, "end": v(-31.85, 12.45) * mm});
            skLineSegment(sketch, "E359", {"start": v(-31.85, 12.45) * mm, "end": v(-27.3, 12.45) * mm});
            skLineSegment(sketch, "E360", {"start": v(-27.3, 12.45) * mm, "end": v(-27.3, 18.14) * mm});
            skLineSegment(sketch, "E361", {"start": v(-27.3, 18.14) * mm, "end": v(-26.4, 18.54) * mm});
            skLineSegment(sketch, "E362", {"start": v(-26.4, 18.54) * mm, "end": v(-26.4, 12.45) * mm});
            skLineSegment(sketch, "E363", {"start": v(-26.4, 12.45) * mm, "end": v(-20.82, 12.45) * mm});
            skLineSegment(sketch, "E364", {"start": v(-20.82, 12.45) * mm, "end": v(-20.82, 11.58) * mm});
            skLineSegment(sketch, "E365", {"start": v(-20.82, 11.58) * mm, "end": v(-26.4, 11.58) * mm});
            skLineSegment(sketch, "E366", {"start": v(-26.4, 11.58) * mm, "end": v(-26.4, -1.7) * mm});
            skLineSegment(sketch, "E367", {"start": v(-26.4, -1.7) * mm, "end": v(-26.4, -2.58) * mm});
            skLineSegment(sketch, "E368", {"start": v(-26.4, -2.58) * mm, "end": v(-26.4, -2.78) * mm});
            skLineSegment(sketch, "E369", {"start": v(-26.4, -2.78) * mm, "end": v(-26.38, -2.97) * mm});
            skLineSegment(sketch, "E370", {"start": v(-26.38, -2.97) * mm, "end": v(-26.37, -3.16) * mm});
            skLineSegment(sketch, "E371", {"start": v(-26.37, -3.16) * mm, "end": v(-26.36, -3.34) * mm});
            skLineSegment(sketch, "E372", {"start": v(-26.36, -3.34) * mm, "end": v(-26.34, -3.5) * mm});
            skLineSegment(sketch, "E373", {"start": v(-26.34, -3.5) * mm, "end": v(-26.31, -3.67) * mm});
            skLineSegment(sketch, "E374", {"start": v(-26.31, -3.67) * mm, "end": v(-26.28, -3.82) * mm});
            skLineSegment(sketch, "E375", {"start": v(-26.28, -3.82) * mm, "end": v(-26.25, -3.97) * mm});
            skLineSegment(sketch, "E376", {"start": v(-26.25, -3.97) * mm, "end": v(-26.21, -4.11) * mm});
            skLineSegment(sketch, "E377", {"start": v(-26.21, -4.11) * mm, "end": v(-26.17, -4.24) * mm});
            skLineSegment(sketch, "E378", {"start": v(-26.17, -4.24) * mm, "end": v(-26.13, -4.37) * mm});
            skLineSegment(sketch, "E379", {"start": v(-26.13, -4.37) * mm, "end": v(-26.08, -4.48) * mm});
            skLineSegment(sketch, "E380", {"start": v(-26.08, -4.48) * mm, "end": v(-26.02, -4.6) * mm});
            skLineSegment(sketch, "E381", {"start": v(-26.02, -4.6) * mm, "end": v(-25.96, -4.7) * mm});
            skLineSegment(sketch, "E382", {"start": v(-25.96, -4.7) * mm, "end": v(-25.9, -4.79) * mm});
            skLineSegment(sketch, "E383", {"start": v(-25.9, -4.79) * mm, "end": v(-25.83, -4.87) * mm});
            skLineSegment(sketch, "E384", {"start": v(-25.83, -4.87) * mm, "end": v(-25.76, -4.95) * mm});
            skLineSegment(sketch, "E385", {"start": v(-25.76, -4.95) * mm, "end": v(-25.68, -5.03) * mm});
            skLineSegment(sketch, "E386", {"start": v(-25.68, -5.03) * mm, "end": v(-25.6, -5.1) * mm});
            skLineSegment(sketch, "E387", {"start": v(-25.6, -5.1) * mm, "end": v(-25.5, -5.16) * mm});
            skLineSegment(sketch, "E388", {"start": v(-25.5, -5.16) * mm, "end": v(-25.4, -5.22) * mm});
            skLineSegment(sketch, "E389", {"start": v(-25.4, -5.22) * mm, "end": v(-25.29, -5.27) * mm});
            skLineSegment(sketch, "E390", {"start": v(-25.29, -5.27) * mm, "end": v(-25.17, -5.32) * mm});
            skLineSegment(sketch, "E391", {"start": v(-25.17, -5.32) * mm, "end": v(-25.04, -5.37) * mm});
            skLineSegment(sketch, "E392", {"start": v(-25.04, -5.37) * mm, "end": v(-24.9, -5.4) * mm});
            skLineSegment(sketch, "E393", {"start": v(-24.9, -5.4) * mm, "end": v(-24.75, -5.44) * mm});
            skLineSegment(sketch, "E394", {"start": v(-24.75, -5.44) * mm, "end": v(-24.6, -5.47) * mm});
            skLineSegment(sketch, "E395", {"start": v(-24.6, -5.47) * mm, "end": v(-24.43, -5.49) * mm});
            skLineSegment(sketch, "E396", {"start": v(-24.43, -5.49) * mm, "end": v(-24.26, -5.5) * mm});
            skLineSegment(sketch, "E397", {"start": v(-24.26, -5.5) * mm, "end": v(-24.08, -5.52) * mm});
            skLineSegment(sketch, "E398", {"start": v(-24.08, -5.52) * mm, "end": v(-23.88, -5.53) * mm});
            skLineSegment(sketch, "E399", {"start": v(-23.88, -5.53) * mm, "end": v(-23.68, -5.53) * mm});
            skLineSegment(sketch, "E400", {"start": v(-23.68, -5.53) * mm, "end": v(-23.53, -5.53) * mm});
            skLineSegment(sketch, "E401", {"start": v(-23.53, -5.53) * mm, "end": v(-21.28, -5.53) * mm});
            skLineSegment(sketch, "E402", {"start": v(-21.28, -5.53) * mm, "end": v(-21.28, -6.4) * mm});
            skLineSegment(sketch, "E403", {"start": v(-21.28, -6.4) * mm, "end": v(-23.53, -6.4) * mm});
            skLineSegment(sketch, "E404", {"start": v(-16.35, 12.45) * mm, "end": v(-16.35, 0.89) * mm});
            skLineSegment(sketch, "E405", {"start": v(-16.35, 0.89) * mm, "end": v(-16.34, 0.48) * mm});
            skLineSegment(sketch, "E406", {"start": v(-16.34, 0.48) * mm, "end": v(-16.32, 0.08) * mm});
            skLineSegment(sketch, "E407", {"start": v(-16.32, 0.08) * mm, "end": v(-16.3, -0.3) * mm});
            skLineSegment(sketch, "E408", {"start": v(-16.3, -0.3) * mm, "end": v(-16.26, -0.68) * mm});
            skLineSegment(sketch, "E409", {"start": v(-16.26, -0.68) * mm, "end": v(-16.2, -1.05) * mm});
            skLineSegment(sketch, "E410", {"start": v(-16.2, -1.05) * mm, "end": v(-16.14, -1.4) * mm});
            skLineSegment(sketch, "E411", {"start": v(-16.14, -1.4) * mm, "end": v(-16.07, -1.74) * mm});
            skLineSegment(sketch, "E412", {"start": v(-16.07, -1.74) * mm, "end": v(-15.98, -2.06) * mm});
            skLineSegment(sketch, "E413", {"start": v(-15.98, -2.06) * mm, "end": v(-15.88, -2.37) * mm});
            skLineSegment(sketch, "E414", {"start": v(-15.88, -2.37) * mm, "end": v(-15.77, -2.68) * mm});
            skLineSegment(sketch, "E415", {"start": v(-15.77, -2.68) * mm, "end": v(-15.65, -2.96) * mm});
            skLineSegment(sketch, "E416", {"start": v(-15.65, -2.96) * mm, "end": v(-15.52, -3.24) * mm});
            skLineSegment(sketch, "E417", {"start": v(-15.52, -3.24) * mm, "end": v(-15.38, -3.5) * mm});
            skLineSegment(sketch, "E418", {"start": v(-15.38, -3.5) * mm, "end": v(-15.22, -3.75) * mm});
            skLineSegment(sketch, "E419", {"start": v(-15.22, -3.75) * mm, "end": v(-15.06, -4) * mm});
            skLineSegment(sketch, "E420", {"start": v(-15.06, -4) * mm, "end": v(-14.88, -4.22) * mm});
            skLineSegment(sketch, "E421", {"start": v(-14.88, -4.22) * mm, "end": v(-14.68, -4.44) * mm});
            skLineSegment(sketch, "E422", {"start": v(-14.68, -4.44) * mm, "end": v(-14.46, -4.64) * mm});
            skLineSegment(sketch, "E423", {"start": v(-14.46, -4.64) * mm, "end": v(-14.23, -4.83) * mm});
            skLineSegment(sketch, "E424", {"start": v(-14.23, -4.83) * mm, "end": v(-14, -5.01) * mm});
            skLineSegment(sketch, "E425", {"start": v(-14, -5.01) * mm, "end": v(-13.74, -5.17) * mm});
            skLineSegment(sketch, "E426", {"start": v(-13.74, -5.17) * mm, "end": v(-13.47, -5.32) * mm});
            skLineSegment(sketch, "E427", {"start": v(-13.47, -5.32) * mm, "end": v(-13.19, -5.46) * mm});
            skLineSegment(sketch, "E428", {"start": v(-13.19, -5.46) * mm, "end": v(-12.9, -5.58) * mm});
            skLineSegment(sketch, "E429", {"start": v(-12.9, -5.58) * mm, "end": v(-12.59, -5.69) * mm});
            skLineSegment(sketch, "E430", {"start": v(-12.59, -5.69) * mm, "end": v(-12.27, -5.78) * mm});
            skLineSegment(sketch, "E431", {"start": v(-12.27, -5.78) * mm, "end": v(-11.94, -5.86) * mm});
            skLineSegment(sketch, "E432", {"start": v(-11.94, -5.86) * mm, "end": v(-11.59, -5.93) * mm});
            skLineSegment(sketch, "E433", {"start": v(-11.59, -5.93) * mm, "end": v(-11.23, -5.98) * mm});
            skLineSegment(sketch, "E434", {"start": v(-11.23, -5.98) * mm, "end": v(-10.85, -6.01) * mm});
            skLineSegment(sketch, "E435", {"start": v(-10.85, -6.01) * mm, "end": v(-10.47, -6.03) * mm});
            skLineSegment(sketch, "E436", {"start": v(-10.47, -6.03) * mm, "end": v(-10.06, -6.04) * mm});
            skLineSegment(sketch, "E437", {"start": v(-10.06, -6.04) * mm, "end": v(-9.71, -6.03) * mm});
            skLineSegment(sketch, "E438", {"start": v(-9.71, -6.03) * mm, "end": v(-9.37, -6.01) * mm});
            skLineSegment(sketch, "E439", {"start": v(-9.37, -6.01) * mm, "end": v(-9.03, -5.97) * mm});
            skLineSegment(sketch, "E440", {"start": v(-9.03, -5.97) * mm, "end": v(-8.7, -5.92) * mm});
            skLineSegment(sketch, "E441", {"start": v(-8.7, -5.92) * mm, "end": v(-8.38, -5.85) * mm});
            skLineSegment(sketch, "E442", {"start": v(-8.38, -5.85) * mm, "end": v(-8.06, -5.76) * mm});
            skLineSegment(sketch, "E443", {"start": v(-8.06, -5.76) * mm, "end": v(-7.75, -5.66) * mm});
            skLineSegment(sketch, "E444", {"start": v(-7.75, -5.66) * mm, "end": v(-7.45, -5.55) * mm});
            skLineSegment(sketch, "E445", {"start": v(-7.45, -5.55) * mm, "end": v(-7.15, -5.42) * mm});
            skLineSegment(sketch, "E446", {"start": v(-7.15, -5.42) * mm, "end": v(-6.86, -5.27) * mm});
            skLineSegment(sketch, "E447", {"start": v(-6.86, -5.27) * mm, "end": v(-6.58, -5.11) * mm});
            skLineSegment(sketch, "E448", {"start": v(-6.58, -5.11) * mm, "end": v(-6.3, -4.93) * mm});
            skLineSegment(sketch, "E449", {"start": v(-6.3, -4.93) * mm, "end": v(-6.04, -4.74) * mm});
            skLineSegment(sketch, "E450", {"start": v(-6.04, -4.74) * mm, "end": v(-5.78, -4.53) * mm});
            skLineSegment(sketch, "E451", {"start": v(-5.78, -4.53) * mm, "end": v(-5.53, -4.31) * mm});
            skLineSegment(sketch, "E452", {"start": v(-5.53, -4.31) * mm, "end": v(-5.29, -4.07) * mm});
            skLineSegment(sketch, "E453", {"start": v(-5.29, -4.07) * mm, "end": v(-5.05, -3.82) * mm});
            skLineSegment(sketch, "E454", {"start": v(-5.05, -3.82) * mm, "end": v(-4.84, -3.56) * mm});
            skLineSegment(sketch, "E455", {"start": v(-4.84, -3.56) * mm, "end": v(-4.63, -3.3) * mm});
            skLineSegment(sketch, "E456", {"start": v(-4.63, -3.3) * mm, "end": v(-4.45, -3.01) * mm});
            skLineSegment(sketch, "E457", {"start": v(-4.45, -3.01) * mm, "end": v(-4.27, -2.72) * mm});
            skLineSegment(sketch, "E458", {"start": v(-4.27, -2.72) * mm, "end": v(-4.12, -2.43) * mm});
            skLineSegment(sketch, "E459", {"start": v(-4.12, -2.43) * mm, "end": v(-3.97, -2.12) * mm});
            skLineSegment(sketch, "E460", {"start": v(-3.97, -2.12) * mm, "end": v(-3.85, -1.8) * mm});
            skLineSegment(sketch, "E461", {"start": v(-3.85, -1.8) * mm, "end": v(-3.73, -1.48) * mm});
            skLineSegment(sketch, "E462", {"start": v(-3.73, -1.48) * mm, "end": v(-3.64, -1.15) * mm});
            skLineSegment(sketch, "E463", {"start": v(-3.64, -1.15) * mm, "end": v(-3.55, -0.8) * mm});
            skLineSegment(sketch, "E464", {"start": v(-3.55, -0.8) * mm, "end": v(-3.49, -0.46) * mm});
            skLineSegment(sketch, "E465", {"start": v(-3.49, -0.46) * mm, "end": v(-3.43, -0.1) * mm});
            skLineSegment(sketch, "E466", {"start": v(-3.43, -0.1) * mm, "end": v(-3.4, 0.27) * mm});
            skLineSegment(sketch, "E467", {"start": v(-3.4, 0.27) * mm, "end": v(-3.37, 0.65) * mm});
            skLineSegment(sketch, "E468", {"start": v(-3.37, 0.65) * mm, "end": v(-3.37, 1.03) * mm});
            skLineSegment(sketch, "E469", {"start": v(-3.37, 1.03) * mm, "end": v(-3.37, 1.75) * mm});
            skLineSegment(sketch, "E470", {"start": v(-3.37, 1.75) * mm, "end": v(-3.37, 12.45) * mm});
            skLineSegment(sketch, "E471", {"start": v(-3.37, 12.45) * mm, "end": v(-2.46, 12.45) * mm});
            skLineSegment(sketch, "E472", {"start": v(-2.46, 12.45) * mm, "end": v(-2.46, -6.4) * mm});
            skLineSegment(sketch, "E473", {"start": v(-2.46, -6.4) * mm, "end": v(-3.37, -6.4) * mm});
            skLineSegment(sketch, "E474", {"start": v(-3.37, -6.4) * mm, "end": v(-3.37, -2.72) * mm});
            skLineSegment(sketch, "E475", {"start": v(-3.37, -2.72) * mm, "end": v(-3.64, -3.23) * mm});
            skLineSegment(sketch, "E476", {"start": v(-3.64, -3.23) * mm, "end": v(-3.94, -3.7) * mm});
            skLineSegment(sketch, "E477", {"start": v(-3.94, -3.7) * mm, "end": v(-4.26, -4.14) * mm});
            skLineSegment(sketch, "E478", {"start": v(-4.26, -4.14) * mm, "end": v(-4.59, -4.55) * mm});
            skLineSegment(sketch, "E479", {"start": v(-4.59, -4.55) * mm, "end": v(-4.94, -4.92) * mm});
            skLineSegment(sketch, "E480", {"start": v(-4.94, -4.92) * mm, "end": v(-5.31, -5.27) * mm});
            skLineSegment(sketch, "E481", {"start": v(-5.31, -5.27) * mm, "end": v(-5.7, -5.58) * mm});
            skLineSegment(sketch, "E482", {"start": v(-5.7, -5.58) * mm, "end": v(-6.1, -5.86) * mm});
            skLineSegment(sketch, "E483", {"start": v(-6.1, -5.86) * mm, "end": v(-6.54, -6.1) * mm});
            skLineSegment(sketch, "E484", {"start": v(-6.54, -6.1) * mm, "end": v(-6.98, -6.32) * mm});
            skLineSegment(sketch, "E485", {"start": v(-6.98, -6.32) * mm, "end": v(-7.45, -6.5) * mm});
            skLineSegment(sketch, "E486", {"start": v(-7.45, -6.5) * mm, "end": v(-7.93, -6.65) * mm});
            skLineSegment(sketch, "E487", {"start": v(-7.93, -6.65) * mm, "end": v(-8.44, -6.77) * mm});
            skLineSegment(sketch, "E488", {"start": v(-8.44, -6.77) * mm, "end": v(-8.96, -6.85) * mm});
            skLineSegment(sketch, "E489", {"start": v(-8.96, -6.85) * mm, "end": v(-9.5, -6.9) * mm});
            skLineSegment(sketch, "E490", {"start": v(-9.5, -6.9) * mm, "end": v(-10.06, -6.92) * mm});
            skLineSegment(sketch, "E491", {"start": v(-10.06, -6.92) * mm, "end": v(-10.94, -6.89) * mm});
            skLineSegment(sketch, "E492", {"start": v(-10.94, -6.89) * mm, "end": v(-11.76, -6.8) * mm});
            skLineSegment(sketch, "E493", {"start": v(-11.76, -6.8) * mm, "end": v(-12.52, -6.64) * mm});
            skLineSegment(sketch, "E494", {"start": v(-12.52, -6.64) * mm, "end": v(-13.22, -6.43) * mm});
            skLineSegment(sketch, "E495", {"start": v(-13.22, -6.43) * mm, "end": v(-13.87, -6.15) * mm});
            skLineSegment(sketch, "E496", {"start": v(-13.87, -6.15) * mm, "end": v(-14.45, -5.81) * mm});
            skLineSegment(sketch, "E497", {"start": v(-14.45, -5.81) * mm, "end": v(-14.99, -5.42) * mm});
            skLineSegment(sketch, "E498", {"start": v(-14.99, -5.42) * mm, "end": v(-15.46, -4.96) * mm});
            skLineSegment(sketch, "E499", {"start": v(-15.46, -4.96) * mm, "end": v(-15.88, -4.44) * mm});
            skLineSegment(sketch, "E500", {"start": v(-15.88, -4.44) * mm, "end": v(-16.25, -3.86) * mm});
            skLineSegment(sketch, "E501", {"start": v(-16.25, -3.86) * mm, "end": v(-16.55, -3.22) * mm});
            skLineSegment(sketch, "E502", {"start": v(-16.55, -3.22) * mm, "end": v(-16.8, -2.52) * mm});
            skLineSegment(sketch, "E503", {"start": v(-16.8, -2.52) * mm, "end": v(-17, -1.76) * mm});
            skLineSegment(sketch, "E504", {"start": v(-17, -1.76) * mm, "end": v(-17.14, -0.93) * mm});
            skLineSegment(sketch, "E505", {"start": v(-17.14, -0.93) * mm, "end": v(-17.22, -0.05) * mm});
            skLineSegment(sketch, "E506", {"start": v(-17.22, -0.05) * mm, "end": v(-17.25, 0.89) * mm});
            skLineSegment(sketch, "E507", {"start": v(-17.25, 0.89) * mm, "end": v(-17.25, 12.45) * mm});
            skLineSegment(sketch, "E508", {"start": v(-17.25, 12.45) * mm, "end": v(-16.35, 12.45) * mm});
            skLineSegment(sketch, "E509", {"start": v(17.66, -6.4) * mm, "end": v(17.66, -1.56) * mm});
            skLineSegment(sketch, "E510", {"start": v(17.66, -1.56) * mm, "end": v(17.4, -2.2) * mm});
            skLineSegment(sketch, "E511", {"start": v(17.4, -2.2) * mm, "end": v(17.1, -2.81) * mm});
            skLineSegment(sketch, "E512", {"start": v(17.1, -2.81) * mm, "end": v(16.78, -3.38) * mm});
            skLineSegment(sketch, "E513", {"start": v(16.78, -3.38) * mm, "end": v(16.44, -3.9) * mm});
            skLineSegment(sketch, "E514", {"start": v(16.44, -3.9) * mm, "end": v(16.06, -4.38) * mm});
            skLineSegment(sketch, "E515", {"start": v(16.06, -4.38) * mm, "end": v(15.66, -4.82) * mm});
            skLineSegment(sketch, "E516", {"start": v(15.66, -4.82) * mm, "end": v(15.24, -5.22) * mm});
            skLineSegment(sketch, "E517", {"start": v(15.24, -5.22) * mm, "end": v(14.78, -5.58) * mm});
            skLineSegment(sketch, "E518", {"start": v(14.78, -5.58) * mm, "end": v(14.3, -5.9) * mm});
            skLineSegment(sketch, "E519", {"start": v(14.3, -5.9) * mm, "end": v(13.8, -6.16) * mm});
            skLineSegment(sketch, "E520", {"start": v(13.8, -6.16) * mm, "end": v(13.26, -6.4) * mm});
            skLineSegment(sketch, "E521", {"start": v(13.26, -6.4) * mm, "end": v(12.7, -6.58) * mm});
            skLineSegment(sketch, "E522", {"start": v(12.7, -6.58) * mm, "end": v(12.1, -6.73) * mm});
            skLineSegment(sketch, "E523", {"start": v(12.1, -6.73) * mm, "end": v(11.5, -6.83) * mm});
            skLineSegment(sketch, "E524", {"start": v(11.5, -6.83) * mm, "end": v(10.85, -6.9) * mm});
            skLineSegment(sketch, "E525", {"start": v(10.85, -6.9) * mm, "end": v(10.18, -6.92) * mm});
            skLineSegment(sketch, "E526", {"start": v(10.18, -6.92) * mm, "end": v(9.66, -6.9) * mm});
            skLineSegment(sketch, "E527", {"start": v(9.66, -6.9) * mm, "end": v(9.16, -6.87) * mm});
            skLineSegment(sketch, "E528", {"start": v(9.16, -6.87) * mm, "end": v(8.68, -6.8) * mm});
            skLineSegment(sketch, "E529", {"start": v(8.68, -6.8) * mm, "end": v(8.2, -6.73) * mm});
            skLineSegment(sketch, "E530", {"start": v(8.2, -6.73) * mm, "end": v(7.75, -6.62) * mm});
            skLineSegment(sketch, "E531", {"start": v(7.75, -6.62) * mm, "end": v(7.31, -6.49) * mm});
            skLineSegment(sketch, "E532", {"start": v(7.31, -6.49) * mm, "end": v(6.9, -6.33) * mm});
            skLineSegment(sketch, "E533", {"start": v(6.9, -6.33) * mm, "end": v(6.48, -6.16) * mm});
            skLineSegment(sketch, "E534", {"start": v(6.48, -6.16) * mm, "end": v(6.09, -5.95) * mm});
            skLineSegment(sketch, "E535", {"start": v(6.09, -5.95) * mm, "end": v(5.7, -5.73) * mm});
            skLineSegment(sketch, "E536", {"start": v(5.7, -5.73) * mm, "end": v(5.34, -5.48) * mm});
            skLineSegment(sketch, "E537", {"start": v(5.34, -5.48) * mm, "end": v(5, -5.2) * mm});
            skLineSegment(sketch, "E538", {"start": v(5, -5.2) * mm, "end": v(4.66, -4.91) * mm});
            skLineSegment(sketch, "E539", {"start": v(4.66, -4.91) * mm, "end": v(4.34, -4.6) * mm});
            skLineSegment(sketch, "E540", {"start": v(4.34, -4.6) * mm, "end": v(4.03, -4.25) * mm});
            skLineSegment(sketch, "E541", {"start": v(4.03, -4.25) * mm, "end": v(3.74, -3.89) * mm});
            skLineSegment(sketch, "E542", {"start": v(3.74, -3.89) * mm, "end": v(3.5, -3.54) * mm});
            skLineSegment(sketch, "E543", {"start": v(3.5, -3.54) * mm, "end": v(3.26, -3.18) * mm});
            skLineSegment(sketch, "E544", {"start": v(3.26, -3.18) * mm, "end": v(3.04, -2.81) * mm});
            skLineSegment(sketch, "E545", {"start": v(3.04, -2.81) * mm, "end": v(2.83, -2.43) * mm});
            skLineSegment(sketch, "E546", {"start": v(2.83, -2.43) * mm, "end": v(2.65, -2.04) * mm});
            skLineSegment(sketch, "E547", {"start": v(2.65, -2.04) * mm, "end": v(2.48, -1.64) * mm});
            skLineSegment(sketch, "E548", {"start": v(2.48, -1.64) * mm, "end": v(2.32, -1.22) * mm});
            skLineSegment(sketch, "E549", {"start": v(2.32, -1.22) * mm, "end": v(2.19, -0.8) * mm});
            skLineSegment(sketch, "E550", {"start": v(2.19, -0.8) * mm, "end": v(2.07, -0.36) * mm});
            skLineSegment(sketch, "E551", {"start": v(2.07, -0.36) * mm, "end": v(1.96, 0.09) * mm});
            skLineSegment(sketch, "E552", {"start": v(1.96, 0.09) * mm, "end": v(1.87, 0.54) * mm});
            skLineSegment(sketch, "E553", {"start": v(1.87, 0.54) * mm, "end": v(1.8, 1.01) * mm});
            skLineSegment(sketch, "E554", {"start": v(1.8, 1.01) * mm, "end": v(1.75, 1.5) * mm});
            skLineSegment(sketch, "E555", {"start": v(1.75, 1.5) * mm, "end": v(1.7, 1.99) * mm});
            skLineSegment(sketch, "E556", {"start": v(1.7, 1.99) * mm, "end": v(1.68, 2.49) * mm});
            skLineSegment(sketch, "E557", {"start": v(1.68, 2.49) * mm, "end": v(1.67, 3) * mm});
            skLineSegment(sketch, "E558", {"start": v(1.67, 3) * mm, "end": v(1.68, 3.52) * mm});
            skLineSegment(sketch, "E559", {"start": v(1.68, 3.52) * mm, "end": v(1.7, 4.02) * mm});
            skLineSegment(sketch, "E560", {"start": v(1.7, 4.02) * mm, "end": v(1.75, 4.51) * mm});
            skLineSegment(sketch, "E561", {"start": v(1.75, 4.51) * mm, "end": v(1.8, 4.99) * mm});
            skLineSegment(sketch, "E562", {"start": v(1.8, 4.99) * mm, "end": v(1.87, 5.46) * mm});
            skLineSegment(sketch, "E563", {"start": v(1.87, 5.46) * mm, "end": v(1.96, 5.91) * mm});
            skLineSegment(sketch, "E564", {"start": v(1.96, 5.91) * mm, "end": v(2.07, 6.36) * mm});
            skLineSegment(sketch, "E565", {"start": v(2.07, 6.36) * mm, "end": v(2.2, 6.79) * mm});
            skLineSegment(sketch, "E566", {"start": v(2.2, 6.79) * mm, "end": v(2.33, 7.21) * mm});
            skLineSegment(sketch, "E567", {"start": v(2.33, 7.21) * mm, "end": v(2.49, 7.62) * mm});
            skLineSegment(sketch, "E568", {"start": v(2.49, 7.62) * mm, "end": v(2.66, 8.02) * mm});
            skLineSegment(sketch, "E569", {"start": v(2.66, 8.02) * mm, "end": v(2.85, 8.41) * mm});
            skLineSegment(sketch, "E570", {"start": v(2.85, 8.41) * mm, "end": v(3.06, 8.79) * mm});
            skLineSegment(sketch, "E571", {"start": v(3.06, 8.79) * mm, "end": v(3.28, 9.16) * mm});
            skLineSegment(sketch, "E572", {"start": v(3.28, 9.16) * mm, "end": v(3.52, 9.51) * mm});
            skLineSegment(sketch, "E573", {"start": v(3.52, 9.51) * mm, "end": v(3.78, 9.86) * mm});
            skLineSegment(sketch, "E574", {"start": v(3.78, 9.86) * mm, "end": v(4.08, 10.24) * mm});
            skLineSegment(sketch, "E575", {"start": v(4.08, 10.24) * mm, "end": v(4.39, 10.6) * mm});
            skLineSegment(sketch, "E576", {"start": v(4.39, 10.6) * mm, "end": v(4.71, 10.92) * mm});
            skLineSegment(sketch, "E577", {"start": v(4.71, 10.92) * mm, "end": v(5.05, 11.22) * mm});
            skLineSegment(sketch, "E578", {"start": v(5.05, 11.22) * mm, "end": v(5.4, 11.5) * mm});
            skLineSegment(sketch, "E579", {"start": v(5.4, 11.5) * mm, "end": v(5.77, 11.76) * mm});
            skLineSegment(sketch, "E580", {"start": v(5.77, 11.76) * mm, "end": v(6.15, 11.99) * mm});
            skLineSegment(sketch, "E581", {"start": v(6.15, 11.99) * mm, "end": v(6.54, 12.2) * mm});
            skLineSegment(sketch, "E582", {"start": v(6.54, 12.2) * mm, "end": v(6.95, 12.37) * mm});
            skLineSegment(sketch, "E583", {"start": v(6.95, 12.37) * mm, "end": v(7.37, 12.53) * mm});
            skLineSegment(sketch, "E584", {"start": v(7.37, 12.53) * mm, "end": v(7.8, 12.66) * mm});
            skLineSegment(sketch, "E585", {"start": v(7.8, 12.66) * mm, "end": v(8.25, 12.77) * mm});
            skLineSegment(sketch, "E586", {"start": v(8.25, 12.77) * mm, "end": v(8.71, 12.85) * mm});
            skLineSegment(sketch, "E587", {"start": v(8.71, 12.85) * mm, "end": v(9.19, 12.91) * mm});
            skLineSegment(sketch, "E588", {"start": v(9.19, 12.91) * mm, "end": v(9.68, 12.95) * mm});
            skLineSegment(sketch, "E589", {"start": v(9.68, 12.95) * mm, "end": v(10.18, 12.96) * mm});
            skLineSegment(sketch, "E590", {"start": v(10.18, 12.96) * mm, "end": v(10.85, 12.94) * mm});
            skLineSegment(sketch, "E591", {"start": v(10.85, 12.94) * mm, "end": v(11.5, 12.88) * mm});
            skLineSegment(sketch, "E592", {"start": v(11.5, 12.88) * mm, "end": v(12.12, 12.77) * mm});
            skLineSegment(sketch, "E593", {"start": v(12.12, 12.77) * mm, "end": v(12.72, 12.63) * mm});
            skLineSegment(sketch, "E594", {"start": v(12.72, 12.63) * mm, "end": v(13.28, 12.44) * mm});
            skLineSegment(sketch, "E595", {"start": v(13.28, 12.44) * mm, "end": v(13.82, 12.2) * mm});
            skLineSegment(sketch, "E596", {"start": v(13.82, 12.2) * mm, "end": v(14.33, 11.93) * mm});
            skLineSegment(sketch, "E597", {"start": v(14.33, 11.93) * mm, "end": v(14.8, 11.62) * mm});
            skLineSegment(sketch, "E598", {"start": v(14.8, 11.62) * mm, "end": v(15.26, 11.26) * mm});
            skLineSegment(sketch, "E599", {"start": v(15.26, 11.26) * mm, "end": v(15.69, 10.86) * mm});
            skLineSegment(sketch, "E600", {"start": v(15.69, 10.86) * mm, "end": v(16.09, 10.42) * mm});
            skLineSegment(sketch, "E601", {"start": v(16.09, 10.42) * mm, "end": v(16.46, 9.93) * mm});
            skLineSegment(sketch, "E602", {"start": v(16.46, 9.93) * mm, "end": v(16.8, 9.4) * mm});
            skLineSegment(sketch, "E603", {"start": v(16.8, 9.4) * mm, "end": v(17.12, 8.83) * mm});
            skLineSegment(sketch, "E604", {"start": v(17.12, 8.83) * mm, "end": v(17.4, 8.22) * mm});
            skLineSegment(sketch, "E605", {"start": v(17.4, 8.22) * mm, "end": v(17.66, 7.56) * mm});
            skLineSegment(sketch, "E606", {"start": v(17.66, 7.56) * mm, "end": v(17.66, 20.15) * mm});
            skLineSegment(sketch, "E607", {"start": v(17.66, 20.15) * mm, "end": v(18.57, 20.15) * mm});
            skLineSegment(sketch, "E608", {"start": v(18.57, 20.15) * mm, "end": v(18.57, -6.4) * mm});
            skLineSegment(sketch, "E609", {"start": v(18.57, -6.4) * mm, "end": v(17.66, -6.4) * mm});
            skLineSegment(sketch, "E610", {"start": v(4.5, 9.35) * mm, "end": v(4.26, 9.04) * mm});
            skLineSegment(sketch, "E611", {"start": v(4.26, 9.04) * mm, "end": v(4.05, 8.71) * mm});
            skLineSegment(sketch, "E612", {"start": v(4.05, 8.71) * mm, "end": v(3.84, 8.38) * mm});
            skLineSegment(sketch, "E613", {"start": v(3.84, 8.38) * mm, "end": v(3.66, 8.03) * mm});
            skLineSegment(sketch, "E614", {"start": v(3.66, 8.03) * mm, "end": v(3.48, 7.67) * mm});
            skLineSegment(sketch, "E615", {"start": v(3.48, 7.67) * mm, "end": v(3.33, 7.3) * mm});
            skLineSegment(sketch, "E616", {"start": v(3.33, 7.3) * mm, "end": v(3.18, 6.92) * mm});
            skLineSegment(sketch, "E617", {"start": v(3.18, 6.92) * mm, "end": v(3.06, 6.53) * mm});
            skLineSegment(sketch, "E618", {"start": v(3.06, 6.53) * mm, "end": v(2.94, 6.13) * mm});
            skLineSegment(sketch, "E619", {"start": v(2.94, 6.13) * mm, "end": v(2.85, 5.72) * mm});
            skLineSegment(sketch, "E620", {"start": v(2.85, 5.72) * mm, "end": v(2.76, 5.3) * mm});
            skLineSegment(sketch, "E621", {"start": v(2.76, 5.3) * mm, "end": v(2.7, 4.86) * mm});
            skLineSegment(sketch, "E622", {"start": v(2.7, 4.86) * mm, "end": v(2.64, 4.41) * mm});
            skLineSegment(sketch, "E623", {"start": v(2.64, 4.41) * mm, "end": v(2.6, 3.95) * mm});
            skLineSegment(sketch, "E624", {"start": v(2.6, 3.95) * mm, "end": v(2.58, 3.48) * mm});
            skLineSegment(sketch, "E625", {"start": v(2.58, 3.48) * mm, "end": v(2.58, 3) * mm});
            skLineSegment(sketch, "E626", {"start": v(2.58, 3) * mm, "end": v(2.58, 2.52) * mm});
            skLineSegment(sketch, "E627", {"start": v(2.58, 2.52) * mm, "end": v(2.6, 2.06) * mm});
            skLineSegment(sketch, "E628", {"start": v(2.6, 2.06) * mm, "end": v(2.64, 1.6) * mm});
            skLineSegment(sketch, "E629", {"start": v(2.64, 1.6) * mm, "end": v(2.7, 1.15) * mm});
            skLineSegment(sketch, "E630", {"start": v(2.7, 1.15) * mm, "end": v(2.76, 0.71) * mm});
            skLineSegment(sketch, "E631", {"start": v(2.76, 0.71) * mm, "end": v(2.84, 0.29) * mm});
            skLineSegment(sketch, "E632", {"start": v(2.84, 0.29) * mm, "end": v(2.93, -0.13) * mm});
            skLineSegment(sketch, "E633", {"start": v(2.93, -0.13) * mm, "end": v(3.04, -0.53) * mm});
            skLineSegment(sketch, "E634", {"start": v(3.04, -0.53) * mm, "end": v(3.16, -0.92) * mm});
            skLineSegment(sketch, "E635", {"start": v(3.16, -0.92) * mm, "end": v(3.3, -1.3) * mm});
            skLineSegment(sketch, "E636", {"start": v(3.3, -1.3) * mm, "end": v(3.46, -1.68) * mm});
            skLineSegment(sketch, "E637", {"start": v(3.46, -1.68) * mm, "end": v(3.62, -2.04) * mm});
            skLineSegment(sketch, "E638", {"start": v(3.62, -2.04) * mm, "end": v(3.8, -2.39) * mm});
            skLineSegment(sketch, "E639", {"start": v(3.8, -2.39) * mm, "end": v(4.01, -2.73) * mm});
            skLineSegment(sketch, "E640", {"start": v(4.01, -2.73) * mm, "end": v(4.23, -3.06) * mm});
            skLineSegment(sketch, "E641", {"start": v(4.23, -3.06) * mm, "end": v(4.46, -3.38) * mm});
            skLineSegment(sketch, "E642", {"start": v(4.46, -3.38) * mm, "end": v(4.72, -3.7) * mm});
            skLineSegment(sketch, "E643", {"start": v(4.72, -3.7) * mm, "end": v(5, -4) * mm});
            skLineSegment(sketch, "E644", {"start": v(5, -4) * mm, "end": v(5.28, -4.27) * mm});
            skLineSegment(sketch, "E645", {"start": v(5.28, -4.27) * mm, "end": v(5.58, -4.53) * mm});
            skLineSegment(sketch, "E646", {"start": v(5.58, -4.53) * mm, "end": v(5.9, -4.77) * mm});
            skLineSegment(sketch, "E647", {"start": v(5.9, -4.77) * mm, "end": v(6.22, -5) * mm});
            skLineSegment(sketch, "E648", {"start": v(6.22, -5) * mm, "end": v(6.56, -5.19) * mm});
            skLineSegment(sketch, "E649", {"start": v(6.56, -5.19) * mm, "end": v(6.9, -5.37) * mm});
            skLineSegment(sketch, "E650", {"start": v(6.9, -5.37) * mm, "end": v(7.27, -5.52) * mm});
            skLineSegment(sketch, "E651", {"start": v(7.27, -5.52) * mm, "end": v(7.65, -5.66) * mm});
            skLineSegment(sketch, "E652", {"start": v(7.65, -5.66) * mm, "end": v(8.04, -5.78) * mm});
            skLineSegment(sketch, "E653", {"start": v(8.04, -5.78) * mm, "end": v(8.44, -5.87) * mm});
            skLineSegment(sketch, "E654", {"start": v(8.44, -5.87) * mm, "end": v(8.86, -5.95) * mm});
            skLineSegment(sketch, "E655", {"start": v(8.86, -5.95) * mm, "end": v(9.28, -6) * mm});
            skLineSegment(sketch, "E656", {"start": v(9.28, -6) * mm, "end": v(9.72, -6.03) * mm});
            skLineSegment(sketch, "E657", {"start": v(9.72, -6.03) * mm, "end": v(10.18, -6.04) * mm});
            skLineSegment(sketch, "E658", {"start": v(10.18, -6.04) * mm, "end": v(10.62, -6.03) * mm});
            skLineSegment(sketch, "E659", {"start": v(10.62, -6.03) * mm, "end": v(11.05, -6) * mm});
            skLineSegment(sketch, "E660", {"start": v(11.05, -6) * mm, "end": v(11.47, -5.95) * mm});
            skLineSegment(sketch, "E661", {"start": v(11.47, -5.95) * mm, "end": v(11.88, -5.88) * mm});
            skLineSegment(sketch, "E662", {"start": v(11.88, -5.88) * mm, "end": v(12.27, -5.79) * mm});
            skLineSegment(sketch, "E663", {"start": v(12.27, -5.79) * mm, "end": v(12.65, -5.67) * mm});
            skLineSegment(sketch, "E664", {"start": v(12.65, -5.67) * mm, "end": v(13.02, -5.54) * mm});
            skLineSegment(sketch, "E665", {"start": v(13.02, -5.54) * mm, "end": v(13.38, -5.39) * mm});
            skLineSegment(sketch, "E666", {"start": v(13.38, -5.39) * mm, "end": v(13.72, -5.22) * mm});
            skLineSegment(sketch, "E667", {"start": v(13.72, -5.22) * mm, "end": v(14.05, -5.02) * mm});
            skLineSegment(sketch, "E668", {"start": v(14.05, -5.02) * mm, "end": v(14.37, -4.81) * mm});
            skLineSegment(sketch, "E669", {"start": v(14.37, -4.81) * mm, "end": v(14.67, -4.58) * mm});
            skLineSegment(sketch, "E670", {"start": v(14.67, -4.58) * mm, "end": v(14.97, -4.33) * mm});
            skLineSegment(sketch, "E671", {"start": v(14.97, -4.33) * mm, "end": v(15.25, -4.06) * mm});
            skLineSegment(sketch, "E672", {"start": v(15.25, -4.06) * mm, "end": v(15.52, -3.76) * mm});
            skLineSegment(sketch, "E673", {"start": v(15.52, -3.76) * mm, "end": v(15.78, -3.45) * mm});
            skLineSegment(sketch, "E674", {"start": v(15.78, -3.45) * mm, "end": v(16, -3.15) * mm});
            skLineSegment(sketch, "E675", {"start": v(16, -3.15) * mm, "end": v(16.22, -2.83) * mm});
            skLineSegment(sketch, "E676", {"start": v(16.22, -2.83) * mm, "end": v(16.42, -2.5) * mm});
            skLineSegment(sketch, "E677", {"start": v(16.42, -2.5) * mm, "end": v(16.6, -2.17) * mm});
            skLineSegment(sketch, "E678", {"start": v(16.6, -2.17) * mm, "end": v(16.77, -1.82) * mm});
            skLineSegment(sketch, "E679", {"start": v(16.77, -1.82) * mm, "end": v(16.92, -1.46) * mm});
            skLineSegment(sketch, "E680", {"start": v(16.92, -1.46) * mm, "end": v(17.06, -1.1) * mm});
            skLineSegment(sketch, "E681", {"start": v(17.06, -1.1) * mm, "end": v(17.19, -0.72) * mm});
            skLineSegment(sketch, "E682", {"start": v(17.19, -0.72) * mm, "end": v(17.3, -0.33) * mm});
            skLineSegment(sketch, "E683", {"start": v(17.3, -0.33) * mm, "end": v(17.4, 0.07) * mm});
            skLineSegment(sketch, "E684", {"start": v(17.4, 0.07) * mm, "end": v(17.48, 0.48) * mm});
            skLineSegment(sketch, "E685", {"start": v(17.48, 0.48) * mm, "end": v(17.54, 0.9) * mm});
            skLineSegment(sketch, "E686", {"start": v(17.54, 0.9) * mm, "end": v(17.6, 1.33) * mm});
            skLineSegment(sketch, "E687", {"start": v(17.6, 1.33) * mm, "end": v(17.63, 1.77) * mm});
            skLineSegment(sketch, "E688", {"start": v(17.63, 1.77) * mm, "end": v(17.66, 2.22) * mm});
            skLineSegment(sketch, "E689", {"start": v(17.66, 2.22) * mm, "end": v(17.66, 2.68) * mm});
            skLineSegment(sketch, "E690", {"start": v(17.66, 2.68) * mm, "end": v(17.66, 2.7) * mm});
            skLineSegment(sketch, "E691", {"start": v(17.66, 2.7) * mm, "end": v(17.66, 2.74) * mm});
            skLineSegment(sketch, "E692", {"start": v(17.66, 2.74) * mm, "end": v(17.66, 2.77) * mm});
            skLineSegment(sketch, "E693", {"start": v(17.66, 2.77) * mm, "end": v(17.66, 2.8) * mm});
            skLineSegment(sketch, "E694", {"start": v(17.66, 2.8) * mm, "end": v(17.66, 2.84) * mm});
            skLineSegment(sketch, "E695", {"start": v(17.66, 2.84) * mm, "end": v(17.66, 2.87) * mm});
            skLineSegment(sketch, "E696", {"start": v(17.66, 2.87) * mm, "end": v(17.66, 2.9) * mm});
            skLineSegment(sketch, "E697", {"start": v(17.66, 2.9) * mm, "end": v(17.66, 2.93) * mm});
            skLineSegment(sketch, "E698", {"start": v(17.66, 2.93) * mm, "end": v(17.66, 2.96) * mm});
            skLineSegment(sketch, "E699", {"start": v(17.66, 2.96) * mm, "end": v(17.66, 3) * mm});
            skLineSegment(sketch, "E700", {"start": v(17.66, 3) * mm, "end": v(17.66, 3.03) * mm});
            skLineSegment(sketch, "E701", {"start": v(17.66, 3.03) * mm, "end": v(17.66, 3.06) * mm});
            skLineSegment(sketch, "E702", {"start": v(17.66, 3.06) * mm, "end": v(17.66, 3.1) * mm});
            skLineSegment(sketch, "E703", {"start": v(17.66, 3.1) * mm, "end": v(17.66, 3.12) * mm});
            skLineSegment(sketch, "E704", {"start": v(17.66, 3.12) * mm, "end": v(17.66, 3.15) * mm});
            skLineSegment(sketch, "E705", {"start": v(17.66, 3.15) * mm, "end": v(17.66, 3.19) * mm});
            skLineSegment(sketch, "E706", {"start": v(17.66, 3.19) * mm, "end": v(17.66, 3.66) * mm});
            skLineSegment(sketch, "E707", {"start": v(17.66, 3.66) * mm, "end": v(17.63, 4.12) * mm});
            skLineSegment(sketch, "E708", {"start": v(17.63, 4.12) * mm, "end": v(17.6, 4.57) * mm});
            skLineSegment(sketch, "E709", {"start": v(17.6, 4.57) * mm, "end": v(17.55, 5.01) * mm});
            skLineSegment(sketch, "E710", {"start": v(17.55, 5.01) * mm, "end": v(17.48, 5.44) * mm});
            skLineSegment(sketch, "E711", {"start": v(17.48, 5.44) * mm, "end": v(17.4, 5.86) * mm});
            skLineSegment(sketch, "E712", {"start": v(17.4, 5.86) * mm, "end": v(17.3, 6.27) * mm});
            skLineSegment(sketch, "E713", {"start": v(17.3, 6.27) * mm, "end": v(17.2, 6.66) * mm});
            skLineSegment(sketch, "E714", {"start": v(17.2, 6.66) * mm, "end": v(17.07, 7.04) * mm});
            skLineSegment(sketch, "E715", {"start": v(17.07, 7.04) * mm, "end": v(16.93, 7.42) * mm});
            skLineSegment(sketch, "E716", {"start": v(16.93, 7.42) * mm, "end": v(16.78, 7.78) * mm});
            skLineSegment(sketch, "E717", {"start": v(16.78, 7.78) * mm, "end": v(16.62, 8.13) * mm});
            skLineSegment(sketch, "E718", {"start": v(16.62, 8.13) * mm, "end": v(16.44, 8.47) * mm});
            skLineSegment(sketch, "E719", {"start": v(16.44, 8.47) * mm, "end": v(16.25, 8.8) * mm});
            skLineSegment(sketch, "E720", {"start": v(16.25, 8.8) * mm, "end": v(16.04, 9.12) * mm});
            skLineSegment(sketch, "E721", {"start": v(16.04, 9.12) * mm, "end": v(15.82, 9.42) * mm});
            skLineSegment(sketch, "E722", {"start": v(15.82, 9.42) * mm, "end": v(15.55, 9.75) * mm});
            skLineSegment(sketch, "E723", {"start": v(15.55, 9.75) * mm, "end": v(15.28, 10.05) * mm});
            skLineSegment(sketch, "E724", {"start": v(15.28, 10.05) * mm, "end": v(14.99, 10.33) * mm});
            skLineSegment(sketch, "E725", {"start": v(14.99, 10.33) * mm, "end": v(14.68, 10.6) * mm});
            skLineSegment(sketch, "E726", {"start": v(14.68, 10.6) * mm, "end": v(14.37, 10.83) * mm});
            skLineSegment(sketch, "E727", {"start": v(14.37, 10.83) * mm, "end": v(14.05, 11.05) * mm});
            skLineSegment(sketch, "E728", {"start": v(14.05, 11.05) * mm, "end": v(13.71, 11.25) * mm});
            skLineSegment(sketch, "E729", {"start": v(13.71, 11.25) * mm, "end": v(13.37, 11.42) * mm});
            skLineSegment(sketch, "E730", {"start": v(13.37, 11.42) * mm, "end": v(13, 11.58) * mm});
            skLineSegment(sketch, "E731", {"start": v(13, 11.58) * mm, "end": v(12.64, 11.71) * mm});
            skLineSegment(sketch, "E732", {"start": v(12.64, 11.71) * mm, "end": v(12.26, 11.83) * mm});
            skLineSegment(sketch, "E733", {"start": v(12.26, 11.83) * mm, "end": v(11.86, 11.92) * mm});
            skLineSegment(sketch, "E734", {"start": v(11.86, 11.92) * mm, "end": v(11.46, 12) * mm});
            skLineSegment(sketch, "E735", {"start": v(11.46, 12) * mm, "end": v(11.04, 12.04) * mm});
            skLineSegment(sketch, "E736", {"start": v(11.04, 12.04) * mm, "end": v(10.62, 12.08) * mm});
            skLineSegment(sketch, "E737", {"start": v(10.62, 12.08) * mm, "end": v(10.18, 12.09) * mm});
            skLineSegment(sketch, "E738", {"start": v(10.18, 12.09) * mm, "end": v(9.73, 12.08) * mm});
            skLineSegment(sketch, "E739", {"start": v(9.73, 12.08) * mm, "end": v(9.3, 12.04) * mm});
            skLineSegment(sketch, "E740", {"start": v(9.3, 12.04) * mm, "end": v(8.87, 11.99) * mm});
            skLineSegment(sketch, "E741", {"start": v(8.87, 11.99) * mm, "end": v(8.46, 11.92) * mm});
            skLineSegment(sketch, "E742", {"start": v(8.46, 11.92) * mm, "end": v(8.07, 11.82) * mm});
            skLineSegment(sketch, "E743", {"start": v(8.07, 11.82) * mm, "end": v(7.68, 11.7) * mm});
            skLineSegment(sketch, "E744", {"start": v(7.68, 11.7) * mm, "end": v(7.3, 11.56) * mm});
            skLineSegment(sketch, "E745", {"start": v(7.3, 11.56) * mm, "end": v(6.94, 11.4) * mm});
            skLineSegment(sketch, "E746", {"start": v(6.94, 11.4) * mm, "end": v(6.6, 11.22) * mm});
            skLineSegment(sketch, "E747", {"start": v(6.6, 11.22) * mm, "end": v(6.25, 11.02) * mm});
            skLineSegment(sketch, "E748", {"start": v(6.25, 11.02) * mm, "end": v(5.93, 10.8) * mm});
            skLineSegment(sketch, "E749", {"start": v(5.93, 10.8) * mm, "end": v(5.62, 10.55) * mm});
            skLineSegment(sketch, "E750", {"start": v(5.62, 10.55) * mm, "end": v(5.32, 10.28) * mm});
            skLineSegment(sketch, "E751", {"start": v(5.32, 10.28) * mm, "end": v(5.03, 10) * mm});
            skLineSegment(sketch, "E752", {"start": v(5.03, 10) * mm, "end": v(4.76, 9.68) * mm});
            skLineSegment(sketch, "E753", {"start": v(4.76, 9.68) * mm, "end": v(4.5, 9.35) * mm});
            skLineSegment(sketch, "E754", {"start": v(25.72, -6.4) * mm, "end": v(24.81, -6.4) * mm});
            skLineSegment(sketch, "E755", {"start": v(24.81, -6.4) * mm, "end": v(24.81, 12.45) * mm});
            skLineSegment(sketch, "E756", {"start": v(24.81, 12.45) * mm, "end": v(25.72, 12.45) * mm});
            skLineSegment(sketch, "E757", {"start": v(25.72, 12.45) * mm, "end": v(25.72, -6.4) * mm});
            skLineSegment(sketch, "E758", {"start": v(46.82, 9.82) * mm, "end": v(47.09, 9.48) * mm});
            skLineSegment(sketch, "E759", {"start": v(47.09, 9.48) * mm, "end": v(47.34, 9.12) * mm});
            skLineSegment(sketch, "E760", {"start": v(47.34, 9.12) * mm, "end": v(47.57, 8.75) * mm});
            skLineSegment(sketch, "E761", {"start": v(47.57, 8.75) * mm, "end": v(47.79, 8.37) * mm});
            skLineSegment(sketch, "E762", {"start": v(47.79, 8.37) * mm, "end": v(47.99, 7.98) * mm});
            skLineSegment(sketch, "E763", {"start": v(47.99, 7.98) * mm, "end": v(48.17, 7.58) * mm});
            skLineSegment(sketch, "E764", {"start": v(48.17, 7.58) * mm, "end": v(48.33, 7.16) * mm});
            skLineSegment(sketch, "E765", {"start": v(48.33, 7.16) * mm, "end": v(48.48, 6.74) * mm});
            skLineSegment(sketch, "E766", {"start": v(48.48, 6.74) * mm, "end": v(48.61, 6.31) * mm});
            skLineSegment(sketch, "E767", {"start": v(48.61, 6.31) * mm, "end": v(48.73, 5.87) * mm});
            skLineSegment(sketch, "E768", {"start": v(48.73, 5.87) * mm, "end": v(48.82, 5.41) * mm});
            skLineSegment(sketch, "E769", {"start": v(48.82, 5.41) * mm, "end": v(48.9, 4.95) * mm});
            skLineSegment(sketch, "E770", {"start": v(48.9, 4.95) * mm, "end": v(48.96, 4.48) * mm});
            skLineSegment(sketch, "E771", {"start": v(48.96, 4.48) * mm, "end": v(49, 4) * mm});
            skLineSegment(sketch, "E772", {"start": v(49, 4) * mm, "end": v(49.03, 3.5) * mm});
            skLineSegment(sketch, "E773", {"start": v(49.03, 3.5) * mm, "end": v(49.04, 3) * mm});
            skLineSegment(sketch, "E774", {"start": v(49.04, 3) * mm, "end": v(49.03, 2.5) * mm});
            skLineSegment(sketch, "E775", {"start": v(49.03, 2.5) * mm, "end": v(49, 2.02) * mm});
            skLineSegment(sketch, "E776", {"start": v(49, 2.02) * mm, "end": v(48.96, 1.55) * mm});
            skLineSegment(sketch, "E777", {"start": v(48.96, 1.55) * mm, "end": v(48.9, 1.08) * mm});
            skLineSegment(sketch, "E778", {"start": v(48.9, 1.08) * mm, "end": v(48.82, 0.62) * mm});
            skLineSegment(sketch, "E779", {"start": v(48.82, 0.62) * mm, "end": v(48.73, 0.18) * mm});
            skLineSegment(sketch, "E780", {"start": v(48.73, 0.18) * mm, "end": v(48.61, -0.26) * mm});
            skLineSegment(sketch, "E781", {"start": v(48.61, -0.26) * mm, "end": v(48.48, -0.7) * mm});
            skLineSegment(sketch, "E782", {"start": v(48.48, -0.7) * mm, "end": v(48.33, -1.11) * mm});
            skLineSegment(sketch, "E783", {"start": v(48.33, -1.11) * mm, "end": v(48.17, -1.53) * mm});
            skLineSegment(sketch, "E784", {"start": v(48.17, -1.53) * mm, "end": v(47.99, -1.93) * mm});
            skLineSegment(sketch, "E785", {"start": v(47.99, -1.93) * mm, "end": v(47.79, -2.33) * mm});
            skLineSegment(sketch, "E786", {"start": v(47.79, -2.33) * mm, "end": v(47.57, -2.71) * mm});
            skLineSegment(sketch, "E787", {"start": v(47.57, -2.71) * mm, "end": v(47.34, -3.09) * mm});
            skLineSegment(sketch, "E788", {"start": v(47.34, -3.09) * mm, "end": v(47.09, -3.46) * mm});
            skLineSegment(sketch, "E789", {"start": v(47.09, -3.46) * mm, "end": v(46.82, -3.82) * mm});
            skLineSegment(sketch, "E790", {"start": v(46.82, -3.82) * mm, "end": v(46.5, -4.19) * mm});
            skLineSegment(sketch, "E791", {"start": v(46.5, -4.19) * mm, "end": v(46.17, -4.54) * mm});
            skLineSegment(sketch, "E792", {"start": v(46.17, -4.54) * mm, "end": v(45.83, -4.86) * mm});
            skLineSegment(sketch, "E793", {"start": v(45.83, -4.86) * mm, "end": v(45.47, -5.16) * mm});
            skLineSegment(sketch, "E794", {"start": v(45.47, -5.16) * mm, "end": v(45.1, -5.44) * mm});
            skLineSegment(sketch, "E795", {"start": v(45.1, -5.44) * mm, "end": v(44.7, -5.7) * mm});
            skLineSegment(sketch, "E796", {"start": v(44.7, -5.7) * mm, "end": v(44.3, -5.93) * mm});
            skLineSegment(sketch, "E797", {"start": v(44.3, -5.93) * mm, "end": v(43.9, -6.13) * mm});
            skLineSegment(sketch, "E798", {"start": v(43.9, -6.13) * mm, "end": v(43.47, -6.32) * mm});
            skLineSegment(sketch, "E799", {"start": v(43.47, -6.32) * mm, "end": v(43.03, -6.47) * mm});
            skLineSegment(sketch, "E800", {"start": v(43.03, -6.47) * mm, "end": v(42.58, -6.6) * mm});
            skLineSegment(sketch, "E801", {"start": v(42.58, -6.6) * mm, "end": v(42.11, -6.72) * mm});
            skLineSegment(sketch, "E802", {"start": v(42.11, -6.72) * mm, "end": v(41.64, -6.8) * mm});
            skLineSegment(sketch, "E803", {"start": v(41.64, -6.8) * mm, "end": v(41.14, -6.87) * mm});
            skLineSegment(sketch, "E804", {"start": v(41.14, -6.87) * mm, "end": v(40.64, -6.9) * mm});
            skLineSegment(sketch, "E805", {"start": v(40.64, -6.9) * mm, "end": v(40.12, -6.92) * mm});
            skLineSegment(sketch, "E806", {"start": v(40.12, -6.92) * mm, "end": v(39.6, -6.9) * mm});
            skLineSegment(sketch, "E807", {"start": v(39.6, -6.9) * mm, "end": v(39.1, -6.87) * mm});
            skLineSegment(sketch, "E808", {"start": v(39.1, -6.87) * mm, "end": v(38.6, -6.8) * mm});
            skLineSegment(sketch, "E809", {"start": v(38.6, -6.8) * mm, "end": v(38.12, -6.72) * mm});
            skLineSegment(sketch, "E810", {"start": v(38.12, -6.72) * mm, "end": v(37.65, -6.6) * mm});
            skLineSegment(sketch, "E811", {"start": v(37.65, -6.6) * mm, "end": v(37.2, -6.47) * mm});
            skLineSegment(sketch, "E812", {"start": v(37.2, -6.47) * mm, "end": v(36.76, -6.32) * mm});
            skLineSegment(sketch, "E813", {"start": v(36.76, -6.32) * mm, "end": v(36.34, -6.13) * mm});
            skLineSegment(sketch, "E814", {"start": v(36.34, -6.13) * mm, "end": v(35.93, -5.93) * mm});
            skLineSegment(sketch, "E815", {"start": v(35.93, -5.93) * mm, "end": v(35.53, -5.7) * mm});
            skLineSegment(sketch, "E816", {"start": v(35.53, -5.7) * mm, "end": v(35.15, -5.44) * mm});
            skLineSegment(sketch, "E817", {"start": v(35.15, -5.44) * mm, "end": v(34.78, -5.16) * mm});
            skLineSegment(sketch, "E818", {"start": v(34.78, -5.16) * mm, "end": v(34.42, -4.86) * mm});
            skLineSegment(sketch, "E819", {"start": v(34.42, -4.86) * mm, "end": v(34.08, -4.54) * mm});
            skLineSegment(sketch, "E820", {"start": v(34.08, -4.54) * mm, "end": v(33.75, -4.19) * mm});
            skLineSegment(sketch, "E821", {"start": v(33.75, -4.19) * mm, "end": v(33.43, -3.82) * mm});
            skLineSegment(sketch, "E822", {"start": v(33.43, -3.82) * mm, "end": v(33.16, -3.46) * mm});
            skLineSegment(sketch, "E823", {"start": v(33.16, -3.46) * mm, "end": v(32.9, -3.09) * mm});
            skLineSegment(sketch, "E824", {"start": v(32.9, -3.09) * mm, "end": v(32.66, -2.71) * mm});
            skLineSegment(sketch, "E825", {"start": v(32.66, -2.71) * mm, "end": v(32.45, -2.33) * mm});
            skLineSegment(sketch, "E826", {"start": v(32.45, -2.33) * mm, "end": v(32.25, -1.93) * mm});
            skLineSegment(sketch, "E827", {"start": v(32.25, -1.93) * mm, "end": v(32.06, -1.53) * mm});
            skLineSegment(sketch, "E828", {"start": v(32.06, -1.53) * mm, "end": v(31.9, -1.11) * mm});
            skLineSegment(sketch, "E829", {"start": v(31.9, -1.11) * mm, "end": v(31.75, -0.7) * mm});
            skLineSegment(sketch, "E830", {"start": v(31.75, -0.7) * mm, "end": v(31.63, -0.26) * mm});
            skLineSegment(sketch, "E831", {"start": v(31.63, -0.26) * mm, "end": v(31.51, 0.18) * mm});
            skLineSegment(sketch, "E832", {"start": v(31.51, 0.18) * mm, "end": v(31.42, 0.62) * mm});
            skLineSegment(sketch, "E833", {"start": v(31.42, 0.62) * mm, "end": v(31.34, 1.08) * mm});
            skLineSegment(sketch, "E834", {"start": v(31.34, 1.08) * mm, "end": v(31.28, 1.55) * mm});
            skLineSegment(sketch, "E835", {"start": v(31.28, 1.55) * mm, "end": v(31.24, 2.02) * mm});
            skLineSegment(sketch, "E836", {"start": v(31.24, 2.02) * mm, "end": v(31.22, 2.5) * mm});
            skLineSegment(sketch, "E837", {"start": v(31.22, 2.5) * mm, "end": v(31.2, 3) * mm});
            skLineSegment(sketch, "E838", {"start": v(31.2, 3) * mm, "end": v(31.22, 3.5) * mm});
            skLineSegment(sketch, "E839", {"start": v(31.22, 3.5) * mm, "end": v(31.24, 4) * mm});
            skLineSegment(sketch, "E840", {"start": v(31.24, 4) * mm, "end": v(31.28, 4.48) * mm});
            skLineSegment(sketch, "E841", {"start": v(31.28, 4.48) * mm, "end": v(31.34, 4.95) * mm});
            skLineSegment(sketch, "E842", {"start": v(31.34, 4.95) * mm, "end": v(31.42, 5.41) * mm});
            skLineSegment(sketch, "E843", {"start": v(31.42, 5.41) * mm, "end": v(31.51, 5.87) * mm});
            skLineSegment(sketch, "E844", {"start": v(31.51, 5.87) * mm, "end": v(31.63, 6.31) * mm});
            skLineSegment(sketch, "E845", {"start": v(31.63, 6.31) * mm, "end": v(31.75, 6.74) * mm});
            skLineSegment(sketch, "E846", {"start": v(31.75, 6.74) * mm, "end": v(31.9, 7.16) * mm});
            skLineSegment(sketch, "E847", {"start": v(31.9, 7.16) * mm, "end": v(32.06, 7.58) * mm});
            skLineSegment(sketch, "E848", {"start": v(32.06, 7.58) * mm, "end": v(32.25, 7.98) * mm});
            skLineSegment(sketch, "E849", {"start": v(32.25, 7.98) * mm, "end": v(32.45, 8.37) * mm});
            skLineSegment(sketch, "E850", {"start": v(32.45, 8.37) * mm, "end": v(32.66, 8.75) * mm});
            skLineSegment(sketch, "E851", {"start": v(32.66, 8.75) * mm, "end": v(32.9, 9.12) * mm});
            skLineSegment(sketch, "E852", {"start": v(32.9, 9.12) * mm, "end": v(33.16, 9.48) * mm});
            skLineSegment(sketch, "E853", {"start": v(33.16, 9.48) * mm, "end": v(33.43, 9.82) * mm});
            skLineSegment(sketch, "E854", {"start": v(33.43, 9.82) * mm, "end": v(33.75, 10.2) * mm});
            skLineSegment(sketch, "E855", {"start": v(33.75, 10.2) * mm, "end": v(34.08, 10.57) * mm});
            skLineSegment(sketch, "E856", {"start": v(34.08, 10.57) * mm, "end": v(34.42, 10.9) * mm});
            skLineSegment(sketch, "E857", {"start": v(34.42, 10.9) * mm, "end": v(34.78, 11.2) * mm});
            skLineSegment(sketch, "E858", {"start": v(34.78, 11.2) * mm, "end": v(35.15, 11.49) * mm});
            skLineSegment(sketch, "E859", {"start": v(35.15, 11.49) * mm, "end": v(35.53, 11.75) * mm});
            skLineSegment(sketch, "E860", {"start": v(35.53, 11.75) * mm, "end": v(35.93, 11.98) * mm});
            skLineSegment(sketch, "E861", {"start": v(35.93, 11.98) * mm, "end": v(36.34, 12.19) * mm});
            skLineSegment(sketch, "E862", {"start": v(36.34, 12.19) * mm, "end": v(36.76, 12.37) * mm});
            skLineSegment(sketch, "E863", {"start": v(36.76, 12.37) * mm, "end": v(37.2, 12.53) * mm});
            skLineSegment(sketch, "E864", {"start": v(37.2, 12.53) * mm, "end": v(37.65, 12.66) * mm});
            skLineSegment(sketch, "E865", {"start": v(37.65, 12.66) * mm, "end": v(38.12, 12.77) * mm});
            skLineSegment(sketch, "E866", {"start": v(38.12, 12.77) * mm, "end": v(38.6, 12.85) * mm});
            skLineSegment(sketch, "E867", {"start": v(38.6, 12.85) * mm, "end": v(39.1, 12.91) * mm});
            skLineSegment(sketch, "E868", {"start": v(39.1, 12.91) * mm, "end": v(39.6, 12.95) * mm});
            skLineSegment(sketch, "E869", {"start": v(39.6, 12.95) * mm, "end": v(40.12, 12.96) * mm});
            skLineSegment(sketch, "E870", {"start": v(40.12, 12.96) * mm, "end": v(40.64, 12.95) * mm});
            skLineSegment(sketch, "E871", {"start": v(40.64, 12.95) * mm, "end": v(41.14, 12.91) * mm});
            skLineSegment(sketch, "E872", {"start": v(41.14, 12.91) * mm, "end": v(41.64, 12.85) * mm});
            skLineSegment(sketch, "E873", {"start": v(41.64, 12.85) * mm, "end": v(42.11, 12.77) * mm});
            skLineSegment(sketch, "E874", {"start": v(42.11, 12.77) * mm, "end": v(42.58, 12.66) * mm});
            skLineSegment(sketch, "E875", {"start": v(42.58, 12.66) * mm, "end": v(43.03, 12.53) * mm});
            skLineSegment(sketch, "E876", {"start": v(43.03, 12.53) * mm, "end": v(43.47, 12.37) * mm});
            skLineSegment(sketch, "E877", {"start": v(43.47, 12.37) * mm, "end": v(43.9, 12.19) * mm});
            skLineSegment(sketch, "E878", {"start": v(43.9, 12.19) * mm, "end": v(44.3, 11.98) * mm});
            skLineSegment(sketch, "E879", {"start": v(44.3, 11.98) * mm, "end": v(44.7, 11.75) * mm});
            skLineSegment(sketch, "E880", {"start": v(44.7, 11.75) * mm, "end": v(45.1, 11.49) * mm});
            skLineSegment(sketch, "E881", {"start": v(45.1, 11.49) * mm, "end": v(45.47, 11.2) * mm});
            skLineSegment(sketch, "E882", {"start": v(45.47, 11.2) * mm, "end": v(45.83, 10.9) * mm});
            skLineSegment(sketch, "E883", {"start": v(45.83, 10.9) * mm, "end": v(46.17, 10.57) * mm});
            skLineSegment(sketch, "E884", {"start": v(46.17, 10.57) * mm, "end": v(46.5, 10.2) * mm});
            skLineSegment(sketch, "E885", {"start": v(46.5, 10.2) * mm, "end": v(46.82, 9.82) * mm});
            skLineSegment(sketch, "E886", {"start": v(34.14, 9.31) * mm, "end": v(33.9, 9) * mm});
            skLineSegment(sketch, "E887", {"start": v(33.9, 9) * mm, "end": v(33.67, 8.66) * mm});
            skLineSegment(sketch, "E888", {"start": v(33.67, 8.66) * mm, "end": v(33.45, 8.32) * mm});
            skLineSegment(sketch, "E889", {"start": v(33.45, 8.32) * mm, "end": v(33.25, 7.97) * mm});
            skLineSegment(sketch, "E890", {"start": v(33.25, 7.97) * mm, "end": v(33.07, 7.61) * mm});
            skLineSegment(sketch, "E891", {"start": v(33.07, 7.61) * mm, "end": v(32.9, 7.24) * mm});
            skLineSegment(sketch, "E892", {"start": v(32.9, 7.24) * mm, "end": v(32.75, 6.86) * mm});
            skLineSegment(sketch, "E893", {"start": v(32.75, 6.86) * mm, "end": v(32.62, 6.47) * mm});
            skLineSegment(sketch, "E894", {"start": v(32.62, 6.47) * mm, "end": v(32.5, 6.07) * mm});
            skLineSegment(sketch, "E895", {"start": v(32.5, 6.07) * mm, "end": v(32.4, 5.66) * mm});
            skLineSegment(sketch, "E896", {"start": v(32.4, 5.66) * mm, "end": v(32.3, 5.24) * mm});
            skLineSegment(sketch, "E897", {"start": v(32.3, 5.24) * mm, "end": v(32.24, 4.82) * mm});
            skLineSegment(sketch, "E898", {"start": v(32.24, 4.82) * mm, "end": v(32.18, 4.38) * mm});
            skLineSegment(sketch, "E899", {"start": v(32.18, 4.38) * mm, "end": v(32.14, 3.93) * mm});
            skLineSegment(sketch, "E900", {"start": v(32.14, 3.93) * mm, "end": v(32.12, 3.47) * mm});
            skLineSegment(sketch, "E901", {"start": v(32.12, 3.47) * mm, "end": v(32.11, 3) * mm});
            skLineSegment(sketch, "E902", {"start": v(32.11, 3) * mm, "end": v(32.12, 2.54) * mm});
            skLineSegment(sketch, "E903", {"start": v(32.12, 2.54) * mm, "end": v(32.14, 2.1) * mm});
            skLineSegment(sketch, "E904", {"start": v(32.14, 2.1) * mm, "end": v(32.18, 1.65) * mm});
            skLineSegment(sketch, "E905", {"start": v(32.18, 1.65) * mm, "end": v(32.24, 1.21) * mm});
            skLineSegment(sketch, "E906", {"start": v(32.24, 1.21) * mm, "end": v(32.3, 0.79) * mm});
            skLineSegment(sketch, "E907", {"start": v(32.3, 0.79) * mm, "end": v(32.4, 0.37) * mm});
            skLineSegment(sketch, "E908", {"start": v(32.4, 0.37) * mm, "end": v(32.5, -0.04) * mm});
            skLineSegment(sketch, "E909", {"start": v(32.5, -0.04) * mm, "end": v(32.62, -0.43) * mm});
            skLineSegment(sketch, "E910", {"start": v(32.62, -0.43) * mm, "end": v(32.75, -0.82) * mm});
            skLineSegment(sketch, "E911", {"start": v(32.75, -0.82) * mm, "end": v(32.9, -1.2) * mm});
            skLineSegment(sketch, "E912", {"start": v(32.9, -1.2) * mm, "end": v(33.07, -1.57) * mm});
            skLineSegment(sketch, "E913", {"start": v(33.07, -1.57) * mm, "end": v(33.25, -1.93) * mm});
            skLineSegment(sketch, "E914", {"start": v(33.25, -1.93) * mm, "end": v(33.45, -2.28) * mm});
            skLineSegment(sketch, "E915", {"start": v(33.45, -2.28) * mm, "end": v(33.67, -2.62) * mm});
            skLineSegment(sketch, "E916", {"start": v(33.67, -2.62) * mm, "end": v(33.9, -2.95) * mm});
            skLineSegment(sketch, "E917", {"start": v(33.9, -2.95) * mm, "end": v(34.14, -3.27) * mm});
            skLineSegment(sketch, "E918", {"start": v(34.14, -3.27) * mm, "end": v(34.42, -3.6) * mm});
            skLineSegment(sketch, "E919", {"start": v(34.42, -3.6) * mm, "end": v(34.72, -3.91) * mm});
            skLineSegment(sketch, "E920", {"start": v(34.72, -3.91) * mm, "end": v(35.02, -4.2) * mm});
            skLineSegment(sketch, "E921", {"start": v(35.02, -4.2) * mm, "end": v(35.34, -4.47) * mm});
            skLineSegment(sketch, "E922", {"start": v(35.34, -4.47) * mm, "end": v(35.67, -4.72) * mm});
            skLineSegment(sketch, "E923", {"start": v(35.67, -4.72) * mm, "end": v(36.02, -4.95) * mm});
            skLineSegment(sketch, "E924", {"start": v(36.02, -4.95) * mm, "end": v(36.37, -5.15) * mm});
            skLineSegment(sketch, "E925", {"start": v(36.37, -5.15) * mm, "end": v(36.74, -5.34) * mm});
            skLineSegment(sketch, "E926", {"start": v(36.74, -5.34) * mm, "end": v(37.12, -5.5) * mm});
            skLineSegment(sketch, "E927", {"start": v(37.12, -5.5) * mm, "end": v(37.51, -5.65) * mm});
            skLineSegment(sketch, "E928", {"start": v(37.51, -5.65) * mm, "end": v(37.92, -5.77) * mm});
            skLineSegment(sketch, "E929", {"start": v(37.92, -5.77) * mm, "end": v(38.33, -5.86) * mm});
            skLineSegment(sketch, "E930", {"start": v(38.33, -5.86) * mm, "end": v(38.76, -5.94) * mm});
            skLineSegment(sketch, "E931", {"start": v(38.76, -5.94) * mm, "end": v(39.2, -6) * mm});
            skLineSegment(sketch, "E932", {"start": v(39.2, -6) * mm, "end": v(39.66, -6.03) * mm});
            skLineSegment(sketch, "E933", {"start": v(39.66, -6.03) * mm, "end": v(40.12, -6.04) * mm});
            skLineSegment(sketch, "E934", {"start": v(40.12, -6.04) * mm, "end": v(40.58, -6.03) * mm});
            skLineSegment(sketch, "E935", {"start": v(40.58, -6.03) * mm, "end": v(41.03, -6) * mm});
            skLineSegment(sketch, "E936", {"start": v(41.03, -6) * mm, "end": v(41.47, -5.94) * mm});
            skLineSegment(sketch, "E937", {"start": v(41.47, -5.94) * mm, "end": v(41.9, -5.86) * mm});
            skLineSegment(sketch, "E938", {"start": v(41.9, -5.86) * mm, "end": v(42.3, -5.77) * mm});
            skLineSegment(sketch, "E939", {"start": v(42.3, -5.77) * mm, "end": v(42.71, -5.65) * mm});
            skLineSegment(sketch, "E940", {"start": v(42.71, -5.65) * mm, "end": v(43.1, -5.5) * mm});
            skLineSegment(sketch, "E941", {"start": v(43.1, -5.5) * mm, "end": v(43.48, -5.34) * mm});
            skLineSegment(sketch, "E942", {"start": v(43.48, -5.34) * mm, "end": v(43.85, -5.15) * mm});
            skLineSegment(sketch, "E943", {"start": v(43.85, -5.15) * mm, "end": v(44.2, -4.95) * mm});
            skLineSegment(sketch, "E944", {"start": v(44.2, -4.95) * mm, "end": v(44.55, -4.72) * mm});
            skLineSegment(sketch, "E945", {"start": v(44.55, -4.72) * mm, "end": v(44.89, -4.47) * mm});
            skLineSegment(sketch, "E946", {"start": v(44.89, -4.47) * mm, "end": v(45.2, -4.2) * mm});
            skLineSegment(sketch, "E947", {"start": v(45.2, -4.2) * mm, "end": v(45.52, -3.91) * mm});
            skLineSegment(sketch, "E948", {"start": v(45.52, -3.91) * mm, "end": v(45.82, -3.6) * mm});
            skLineSegment(sketch, "E949", {"start": v(45.82, -3.6) * mm, "end": v(46.1, -3.27) * mm});
            skLineSegment(sketch, "E950", {"start": v(46.1, -3.27) * mm, "end": v(46.35, -2.95) * mm});
            skLineSegment(sketch, "E951", {"start": v(46.35, -2.95) * mm, "end": v(46.58, -2.62) * mm});
            skLineSegment(sketch, "E952", {"start": v(46.58, -2.62) * mm, "end": v(46.8, -2.28) * mm});
            skLineSegment(sketch, "E953", {"start": v(46.8, -2.28) * mm, "end": v(47, -1.93) * mm});
            skLineSegment(sketch, "E954", {"start": v(47, -1.93) * mm, "end": v(47.18, -1.57) * mm});
            skLineSegment(sketch, "E955", {"start": v(47.18, -1.57) * mm, "end": v(47.35, -1.2) * mm});
            skLineSegment(sketch, "E956", {"start": v(47.35, -1.2) * mm, "end": v(47.5, -0.82) * mm});
            skLineSegment(sketch, "E957", {"start": v(47.5, -0.82) * mm, "end": v(47.63, -0.43) * mm});
            skLineSegment(sketch, "E958", {"start": v(47.63, -0.43) * mm, "end": v(47.75, -0.04) * mm});
            skLineSegment(sketch, "E959", {"start": v(47.75, -0.04) * mm, "end": v(47.85, 0.37) * mm});
            skLineSegment(sketch, "E960", {"start": v(47.85, 0.37) * mm, "end": v(47.94, 0.79) * mm});
            skLineSegment(sketch, "E961", {"start": v(47.94, 0.79) * mm, "end": v(48.01, 1.21) * mm});
            skLineSegment(sketch, "E962", {"start": v(48.01, 1.21) * mm, "end": v(48.07, 1.65) * mm});
            skLineSegment(sketch, "E963", {"start": v(48.07, 1.65) * mm, "end": v(48.1, 2.1) * mm});
            skLineSegment(sketch, "E964", {"start": v(48.1, 2.1) * mm, "end": v(48.13, 2.54) * mm});
            skLineSegment(sketch, "E965", {"start": v(48.13, 2.54) * mm, "end": v(48.14, 3) * mm});
            skLineSegment(sketch, "E966", {"start": v(48.14, 3) * mm, "end": v(48.13, 3.47) * mm});
            skLineSegment(sketch, "E967", {"start": v(48.13, 3.47) * mm, "end": v(48.1, 3.93) * mm});
            skLineSegment(sketch, "E968", {"start": v(48.1, 3.93) * mm, "end": v(48.07, 4.38) * mm});
            skLineSegment(sketch, "E969", {"start": v(48.07, 4.38) * mm, "end": v(48.01, 4.82) * mm});
            skLineSegment(sketch, "E970", {"start": v(48.01, 4.82) * mm, "end": v(47.94, 5.24) * mm});
            skLineSegment(sketch, "E971", {"start": v(47.94, 5.24) * mm, "end": v(47.85, 5.66) * mm});
            skLineSegment(sketch, "E972", {"start": v(47.85, 5.66) * mm, "end": v(47.75, 6.07) * mm});
            skLineSegment(sketch, "E973", {"start": v(47.75, 6.07) * mm, "end": v(47.63, 6.47) * mm});
            skLineSegment(sketch, "E974", {"start": v(47.63, 6.47) * mm, "end": v(47.5, 6.86) * mm});
            skLineSegment(sketch, "E975", {"start": v(47.5, 6.86) * mm, "end": v(47.35, 7.24) * mm});
            skLineSegment(sketch, "E976", {"start": v(47.35, 7.24) * mm, "end": v(47.18, 7.61) * mm});
            skLineSegment(sketch, "E977", {"start": v(47.18, 7.61) * mm, "end": v(47, 7.97) * mm});
            skLineSegment(sketch, "E978", {"start": v(47, 7.97) * mm, "end": v(46.8, 8.32) * mm});
            skLineSegment(sketch, "E979", {"start": v(46.8, 8.32) * mm, "end": v(46.58, 8.66) * mm});
            skLineSegment(sketch, "E980", {"start": v(46.58, 8.66) * mm, "end": v(46.35, 9) * mm});
            skLineSegment(sketch, "E981", {"start": v(46.35, 9) * mm, "end": v(46.1, 9.31) * mm});
            skLineSegment(sketch, "E982", {"start": v(46.1, 9.31) * mm, "end": v(45.82, 9.65) * mm});
            skLineSegment(sketch, "E983", {"start": v(45.82, 9.65) * mm, "end": v(45.52, 9.97) * mm});
            skLineSegment(sketch, "E984", {"start": v(45.52, 9.97) * mm, "end": v(45.2, 10.26) * mm});
            skLineSegment(sketch, "E985", {"start": v(45.2, 10.26) * mm, "end": v(44.89, 10.53) * mm});
            skLineSegment(sketch, "E986", {"start": v(44.89, 10.53) * mm, "end": v(44.55, 10.78) * mm});
            skLineSegment(sketch, "E987", {"start": v(44.55, 10.78) * mm, "end": v(44.2, 11) * mm});
            skLineSegment(sketch, "E988", {"start": v(44.2, 11) * mm, "end": v(43.85, 11.21) * mm});
            skLineSegment(sketch, "E989", {"start": v(43.85, 11.21) * mm, "end": v(43.48, 11.4) * mm});
            skLineSegment(sketch, "E990", {"start": v(43.48, 11.4) * mm, "end": v(43.1, 11.56) * mm});
            skLineSegment(sketch, "E991", {"start": v(43.1, 11.56) * mm, "end": v(42.71, 11.7) * mm});
            skLineSegment(sketch, "E992", {"start": v(42.71, 11.7) * mm, "end": v(42.3, 11.82) * mm});
            skLineSegment(sketch, "E993", {"start": v(42.3, 11.82) * mm, "end": v(41.9, 11.91) * mm});
            skLineSegment(sketch, "E994", {"start": v(41.9, 11.91) * mm, "end": v(41.47, 11.99) * mm});
            skLineSegment(sketch, "E995", {"start": v(41.47, 11.99) * mm, "end": v(41.03, 12.04) * mm});
            skLineSegment(sketch, "E996", {"start": v(41.03, 12.04) * mm, "end": v(40.58, 12.08) * mm});
            skLineSegment(sketch, "E997", {"start": v(40.58, 12.08) * mm, "end": v(40.12, 12.09) * mm});
            skLineSegment(sketch, "E998", {"start": v(40.12, 12.09) * mm, "end": v(39.66, 12.08) * mm});
            skLineSegment(sketch, "E999", {"start": v(39.66, 12.08) * mm, "end": v(39.2, 12.04) * mm});
            skLineSegment(sketch, "E1000", {"start": v(39.2, 12.04) * mm, "end": v(38.76, 11.99) * mm});
            skLineSegment(sketch, "E1001", {"start": v(38.76, 11.99) * mm, "end": v(38.33, 11.91) * mm});
            skLineSegment(sketch, "E1002", {"start": v(38.33, 11.91) * mm, "end": v(37.92, 11.82) * mm});
            skLineSegment(sketch, "E1003", {"start": v(37.92, 11.82) * mm, "end": v(37.51, 11.7) * mm});
            skLineSegment(sketch, "E1004", {"start": v(37.51, 11.7) * mm, "end": v(37.12, 11.56) * mm});
            skLineSegment(sketch, "E1005", {"start": v(37.12, 11.56) * mm, "end": v(36.74, 11.4) * mm});
            skLineSegment(sketch, "E1006", {"start": v(36.74, 11.4) * mm, "end": v(36.37, 11.21) * mm});
            skLineSegment(sketch, "E1007", {"start": v(36.37, 11.21) * mm, "end": v(36.02, 11) * mm});
            skLineSegment(sketch, "E1008", {"start": v(36.02, 11) * mm, "end": v(35.67, 10.78) * mm});
            skLineSegment(sketch, "E1009", {"start": v(35.67, 10.78) * mm, "end": v(35.34, 10.53) * mm});
            skLineSegment(sketch, "E1010", {"start": v(35.34, 10.53) * mm, "end": v(35.02, 10.26) * mm});
            skLineSegment(sketch, "E1011", {"start": v(35.02, 10.26) * mm, "end": v(34.72, 9.97) * mm});
            skLineSegment(sketch, "E1012", {"start": v(34.72, 9.97) * mm, "end": v(34.42, 9.65) * mm});
            skLineSegment(sketch, "E1013", {"start": v(34.42, 9.65) * mm, "end": v(34.14, 9.31) * mm});
            skLineSegment(sketch, "E1014", {"start": v(41.1, -19.7) * mm, "end": v(41.1, -19.79) * mm});
            skLineSegment(sketch, "E1015", {"start": v(41.1, -19.79) * mm, "end": v(41.07, -19.87) * mm});
            skLineSegment(sketch, "E1016", {"start": v(41.07, -19.87) * mm, "end": v(41.03, -19.95) * mm});
            skLineSegment(sketch, "E1017", {"start": v(41.03, -19.95) * mm, "end": v(40.98, -20.02) * mm});
            skLineSegment(sketch, "E1018", {"start": v(40.98, -20.02) * mm, "end": v(40.9, -20.07) * mm});
            skLineSegment(sketch, "E1019", {"start": v(40.9, -20.07) * mm, "end": v(40.83, -20.11) * mm});
            skLineSegment(sketch, "E1020", {"start": v(40.83, -20.11) * mm, "end": v(40.75, -20.14) * mm});
            skLineSegment(sketch, "E1021", {"start": v(40.75, -20.14) * mm, "end": v(40.66, -20.15) * mm});
            skLineSegment(sketch, "E1022", {"start": v(40.66, -20.15) * mm, "end": v(-40.28, -20.15) * mm});
            skLineSegment(sketch, "E1023", {"start": v(-40.28, -20.15) * mm, "end": v(-40.37, -20.14) * mm});
            skLineSegment(sketch, "E1024", {"start": v(-40.37, -20.14) * mm, "end": v(-40.46, -20.11) * mm});
            skLineSegment(sketch, "E1025", {"start": v(-40.46, -20.11) * mm, "end": v(-40.53, -20.07) * mm});
            skLineSegment(sketch, "E1026", {"start": v(-40.53, -20.07) * mm, "end": v(-40.6, -20.02) * mm});
            skLineSegment(sketch, "E1027", {"start": v(-40.6, -20.02) * mm, "end": v(-40.65, -19.95) * mm});
            skLineSegment(sketch, "E1028", {"start": v(-40.65, -19.95) * mm, "end": v(-40.7, -19.87) * mm});
            skLineSegment(sketch, "E1029", {"start": v(-40.7, -19.87) * mm, "end": v(-40.72, -19.79) * mm});
            skLineSegment(sketch, "E1030", {"start": v(-40.72, -19.79) * mm, "end": v(-40.73, -19.7) * mm});
            skLineSegment(sketch, "E1031", {"start": v(-40.73, -19.7) * mm, "end": v(-40.73, -11.32) * mm});
            skLineSegment(sketch, "E1032", {"start": v(-40.73, -11.32) * mm, "end": v(-48.53, -11.32) * mm});
            skLineSegment(sketch, "E1033", {"start": v(-48.53, -11.32) * mm, "end": v(-48.53, -10.34) * mm});
            skLineSegment(sketch, "E1034", {"start": v(-48.53, -10.34) * mm, "end": v(48.9, -10.34) * mm});
            skLineSegment(sketch, "E1035", {"start": v(48.9, -10.34) * mm, "end": v(48.9, -11.32) * mm});
            skLineSegment(sketch, "E1036", {"start": v(48.9, -11.32) * mm, "end": v(41.1, -11.32) * mm});
            skLineSegment(sketch, "E1037", {"start": v(41.1, -11.32) * mm, "end": v(41.1, -19.7) * mm});
            skLineSegment(sketch, "E1038", {"start": v(24.06, 17.41) * mm, "end": v(24.15, 17.88) * mm});
            skLineSegment(sketch, "E1039", {"start": v(24.15, 17.88) * mm, "end": v(24.41, 18.26) * mm});
            skLineSegment(sketch, "E1040", {"start": v(24.41, 18.26) * mm, "end": v(24.8, 18.52) * mm});
            skLineSegment(sketch, "E1041", {"start": v(24.8, 18.52) * mm, "end": v(25.26, 18.62) * mm});
            skLineSegment(sketch, "E1042", {"start": v(25.26, 18.62) * mm, "end": v(25.73, 18.52) * mm});
            skLineSegment(sketch, "E1043", {"start": v(25.73, 18.52) * mm, "end": v(26.12, 18.26) * mm});
            skLineSegment(sketch, "E1044", {"start": v(26.12, 18.26) * mm, "end": v(26.37, 17.88) * mm});
            skLineSegment(sketch, "E1045", {"start": v(26.37, 17.88) * mm, "end": v(26.47, 17.41) * mm});
            skLineSegment(sketch, "E1046", {"start": v(26.47, 17.41) * mm, "end": v(26.37, 16.94) * mm});
            skLineSegment(sketch, "E1047", {"start": v(26.37, 16.94) * mm, "end": v(26.12, 16.56) * mm});
            skLineSegment(sketch, "E1048", {"start": v(26.12, 16.56) * mm, "end": v(25.73, 16.3) * mm});
            skLineSegment(sketch, "E1049", {"start": v(25.73, 16.3) * mm, "end": v(25.26, 16.2) * mm});
            skLineSegment(sketch, "E1050", {"start": v(25.26, 16.2) * mm, "end": v(24.8, 16.3) * mm});
            skLineSegment(sketch, "E1051", {"start": v(24.8, 16.3) * mm, "end": v(24.41, 16.56) * mm});
            skLineSegment(sketch, "E1052", {"start": v(24.41, 16.56) * mm, "end": v(24.15, 16.94) * mm});
            skLineSegment(sketch, "E1053", {"start": v(24.15, 16.94) * mm, "end": v(24.06, 17.41) * mm});
            skSolve(sketch);
        }
        {
            var Q0;
            Q0=makeQuery(id+"F0.imprint","IMPRINT",FACE,{"disambiguationData":[TD([[makeQuery(id+"F0.imprint","IMPRINT",EDGE,{"derivedFrom":sQuery(id+"F0.wireOp",EDGE,"E322")}),-1.0]])]});
            var Q1;
            Q1=makeQuery(id+"F0.imprint","IMPRINT",FACE,{"disambiguationData":[TD([[makeQuery(id+"F0.imprint","IMPRINT",EDGE,{"derivedFrom":sQuery(id+"F0.wireOp",EDGE,"E404")}),-1.0]])]});
            var Q2;
            Q2=makeQuery(id+"F0.imprint","IMPRINT",FACE,{"disambiguationData":[TD([[makeQuery(id+"F0.imprint","IMPRINT",EDGE,{"derivedFrom":sQuery(id+"F0.wireOp",EDGE,"E509")}),-1.0]])]});
            var Q3;
            Q3=makeQuery(id+"F0.imprint","IMPRINT",FACE,{"disambiguationData":[TD([[makeQuery(id+"F0.imprint","IMPRINT",EDGE,{"derivedFrom":sQuery(id+"F0.wireOp",EDGE,"E1038")}),-1.0]])]});
            var Q4;
            Q4=makeQuery(id+"F0.imprint","IMPRINT",FACE,{"disambiguationData":[TD([[makeQuery(id+"F0.imprint","IMPRINT",EDGE,{"derivedFrom":sQuery(id+"F0.wireOp",EDGE,"E754")}),-1.0]])]});
            var Q5;
            Q5=makeQuery(id+"F0.imprint","IMPRINT",FACE,{"disambiguationData":[TD([[makeQuery(id+"F0.imprint","IMPRINT",EDGE,{"derivedFrom":sQuery(id+"F0.wireOp",EDGE,"E1014")}),-1.0]])]});
            var Q6;
            Q6=makeQuery(id+"F0.imprint","IMPRINT",FACE,{"disambiguationData":[TD([[makeQuery(id+"F0.imprint","IMPRINT",EDGE,{"derivedFrom":sQuery(id+"F0.wireOp",EDGE,"E758")}),-1.0]])]});
            var Q7;
            Q7=makeQuery(id+"F0.imprint","IMPRINT",FACE,{"disambiguationData":[TD([[makeQuery(id+"F0.imprint","IMPRINT",EDGE,{"derivedFrom":sQuery(id+"F0.wireOp",EDGE,"E0")}),-1.0]])]});
            extrude(context, id + "F1", {"entities" : qUnion([Q0, Q1, Q2, Q3, Q4, Q5, Q6, Q7]), "depth" : 3 * mm, "offsetDistance" : 25 * mm});
        }
        {
            var Q0;
            Q0=makeQuery(id+"F1.opExtrude","CAP_FACE",FACE,{"disambiguationData":[OSD([sQuery(id+"F0.wireOp",EDGE,"E1014"),sQuery(id+"F0.wireOp",EDGE,"E1015"),sQuery(id+"F0.wireOp",EDGE,"E1016"),sQuery(id+"F0.wireOp",EDGE,"E1017"),sQuery(id+"F0.wireOp",EDGE,"E1018"),sQuery(id+"F0.wireOp",EDGE,"E1019"),sQuery(id+"F0.wireOp",EDGE,"E1020"),sQuery(id+"F0.wireOp",EDGE,"E1021"),sQuery(id+"F0.wireOp",EDGE,"E1022"),sQuery(id+"F0.wireOp",EDGE,"E1023"),sQuery(id+"F0.wireOp",EDGE,"E1024"),sQuery(id+"F0.wireOp",EDGE,"E1025"),sQuery(id+"F0.wireOp",EDGE,"E1026"),sQuery(id+"F0.wireOp",EDGE,"E1027"),sQuery(id+"F0.wireOp",EDGE,"E1028"),sQuery(id+"F0.wireOp",EDGE,"E1029"),sQuery(id+"F0.wireOp",EDGE,"E1030"),sQuery(id+"F0.wireOp",EDGE,"E1031"),sQuery(id+"F0.wireOp",EDGE,"E1032"),sQuery(id+"F0.wireOp",EDGE,"E1033"),sQuery(id+"F0.wireOp",EDGE,"E1034"),sQuery(id+"F0.wireOp",EDGE,"E1035"),sQuery(id+"F0.wireOp",EDGE,"E1036"),sQuery(id+"F0.wireOp",EDGE,"E1037")])],"isStart":true});
            var sketch = newSketch(context, id + "F2", { "sketchPlane" : qUnion([Q0])});
            skLineSegment(sketch, "E1054.bottom", {"start": v(57, -51.5) * mm, "end": v(-57, -51.5) * mm});
            skLineSegment(sketch, "E1054.top", {"start": v(57, 51.5) * mm, "end": v(-57, 51.5) * mm});
            skLineSegment(sketch, "E1054.left", {"start": v(57, -51.5) * mm, "end": v(57, 51.5) * mm});
            skLineSegment(sketch, "E1054.right", {"start": v(-57, -51.5) * mm, "end": v(-57, 51.5) * mm});
            skPoint(sketch, "E1054.middle", {"position": v(0, 0) * mm});
            skSolve(sketch);
        }
        {
            var Q0;
            Q0 = qSketchRegion(id + "F2", true);
            extrude(context, id + "F3", {"entities" : qUnion([Q0]), "operationType" : NewBodyOperationType.ADD, "depth" : 33 * mm, "offsetDistance" : 25 * mm});
        }
    });
